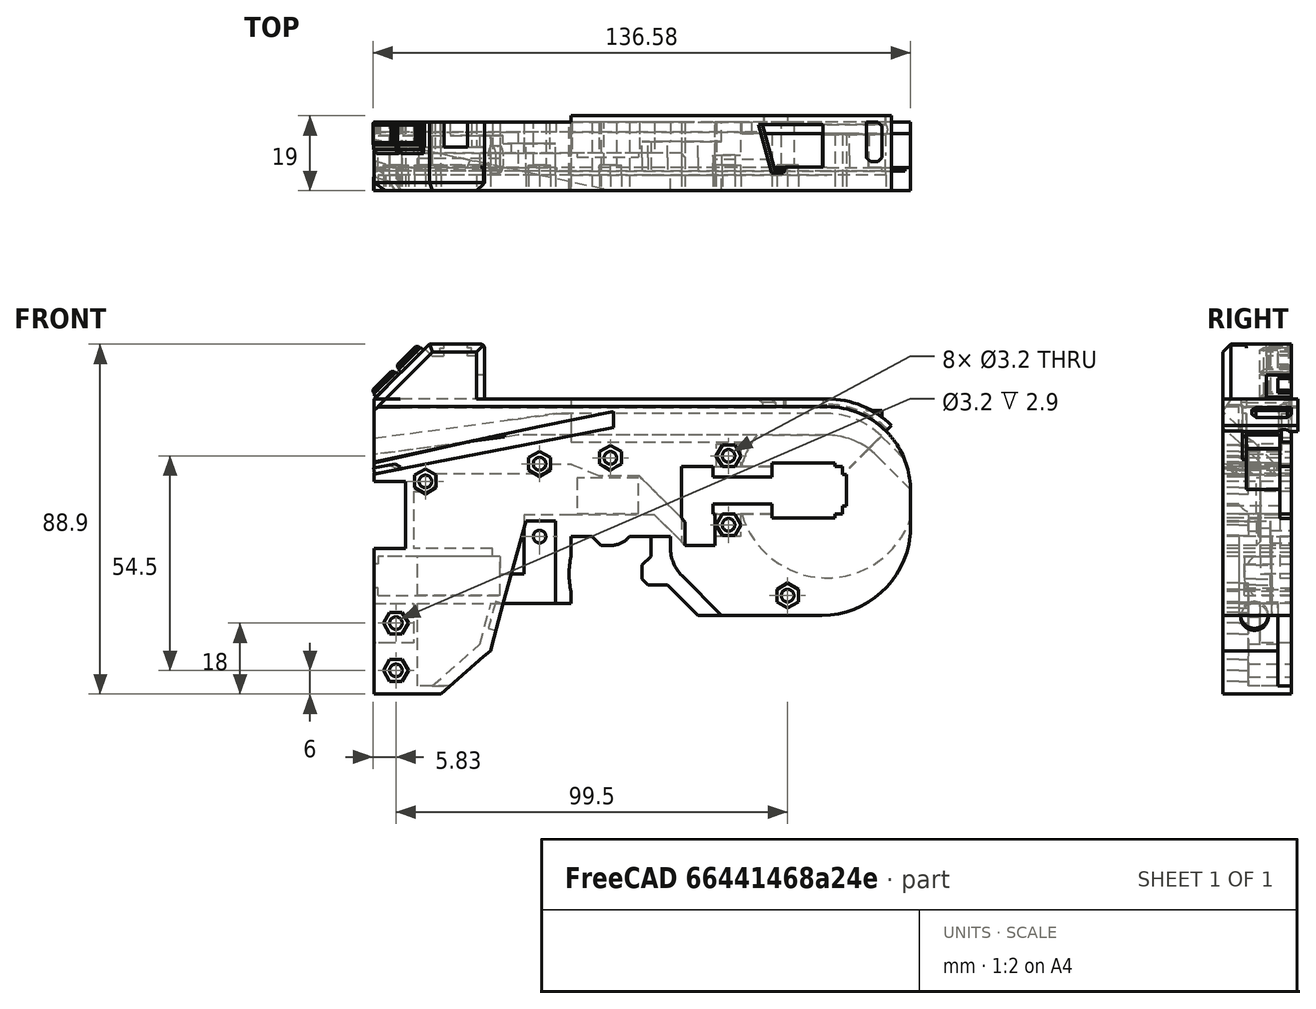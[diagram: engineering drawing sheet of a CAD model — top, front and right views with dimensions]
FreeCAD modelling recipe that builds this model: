
FCSTD DOCUMENT  (FreeCAD 0.20R29603 (Git))
Label: frame
License: All rights reserved
LicenseURL: http://en.wikipedia.org/wiki/All_rights_reserved
objects: Sketcher::SketchObject×74, PartDesign::Pocket×73, PartDesign::Pad×30, PartDesign::Plane×10, PartDesign::Chamfer×10, PartDesign::Groove×4, PartDesign::Fillet×3, PartDesign::Body×1
note: 325 computed .brp shape members not serialized (recipe doc carries the construction recipe); baked Part::Feature solids carry a one-line shape summary decoded from their .brp

FEATURE [Sketcher::SketchObject] Sketch
  FullyConstrained = true
  MapMode = 5
  Placement = pos=(0,0,0) rot=(1,0,0;1.5708rad)
  Support = -> [XZ_Plane]
  sketch-geometry (25):
    g0: LineSegment StartX=32.25 StartY=-20 StartZ=0 EndX=86.25 EndY=-20 EndZ=0
    g1: LineSegment StartX=65 StartY=33 StartZ=0 EndX=-50 EndY=33 EndZ=0
    g2: LineSegment StartX=-50 StartY=33 StartZ=0 EndX=-50 EndY=-40 EndZ=0
    g3: ArcOfCircle CenterX=65 CenterY=11.75 CenterZ=0 NormalX=0 NormalY=0 NormalZ=1 AngleXU=0 Radius=21.25 StartAngle=6.28319 EndAngle=7.85398
    g4: LineSegment StartX=86.25 StartY=11.75 StartZ=0 EndX=86.25 EndY=-20 EndZ=0
    g5: LineSegment StartX=1.8e-15 StartY=0 StartZ=0 EndX=5.375 EndY=0 EndZ=0
    g6: LineSegment StartX=5.375 StartY=0 StartZ=0 EndX=7.625 EndY=-2.25 EndZ=0
    g7: LineSegment StartX=7.625 StartY=-2.25 StartZ=0 EndX=12.625 EndY=-2.25 EndZ=0
    g8: LineSegment StartX=12.625 StartY=-2.25 StartZ=0 EndX=14.875 EndY=0 EndZ=0
    g9: LineSegment StartX=14.875 StartY=0 StartZ=0 EndX=20.25 EndY=0 EndZ=0
    g10: LineSegment StartX=20.25 StartY=0 StartZ=0 EndX=20.25 EndY=-5 EndZ=0
    g11: LineSegment StartX=20.25 StartY=-5 StartZ=0 EndX=18 EndY=-7.25 EndZ=0
    g12: LineSegment StartX=18 StartY=-7.25 StartZ=0 EndX=18 EndY=-10.75 EndZ=0
    g13: LineSegment StartX=18 StartY=-10.75 StartZ=0 EndX=19.5 EndY=-12.25 EndZ=0
    g14: LineSegment StartX=19.5 StartY=-12.25 StartZ=0 EndX=24.5 EndY=-12.25 EndZ=0
    g15: LineSegment StartX=24.5 StartY=-12.25 StartZ=0 EndX=32.25 EndY=-20 EndZ=0
    g16: LineSegment StartX=1.8e-15 StartY=0 StartZ=0 EndX=1.8e-15 EndY=-4 EndZ=0
    g17: ArcOfCircle CenterX=-10 CenterY=-4.5 CenterZ=0 NormalX=0 NormalY=0 NormalZ=1 AngleXU=0 Radius=10.0125 StartAngle=6.23323 EndAngle=6.33314
    g18: ArcOfCircle CenterX=20 CenterY=-9.5 CenterZ=0 NormalX=0 NormalY=0 NormalZ=1 AngleXU=0 Radius=20.5 StartAngle=2.92028 EndAngle=3.36291
    g19: LineSegment StartX=-50 StartY=-40 StartZ=0 EndX=0 EndY=-40 EndZ=0
    g20: LineSegment StartX=0 StartY=-14 StartZ=0 EndX=0 EndY=-40 EndZ=0
    g21: Circle CenterX=-44.5 CenterY=-34 CenterZ=0 NormalX=0 NormalY=0 NormalZ=1 AngleXU=0 Radius=1.6
    g22: Circle CenterX=-8 CenterY=1.1e-15 CenterZ=0 NormalX=0 NormalY=0 NormalZ=1 AngleXU=0 Radius=1.6
    g23: Circle CenterX=-37 CenterY=14 CenterZ=0 NormalX=0 NormalY=0 NormalZ=1 AngleXU=0 Radius=1.6
    g24: Circle CenterX=-8 CenterY=18.5 CenterZ=0 NormalX=0 NormalY=0 NormalZ=1 AngleXU=0 Radius=1.6
  constraints (78):
    c: PointOnObject(g9,g-1)
    c: Horizontal(g0)
    c: Horizontal(g1)
    c: Coincident(g1,g2)
    c: Vertical(g2)
    c: DistanceX(g-1,g9) = 20.25
    c: DistanceY(g0,g9) = 20
    c: DistanceY(g-1,g1) = 33
    c: Coincident(g4,g3)
    c: Coincident(g4,g0)
    c: Vertical(g4)
    c: Coincident(g1,g3)
    c: Tangent(g1,g3)
    c: DistanceX(g-1,g3) = 65
    c: Tangent(g3,g4)
    c: DistanceY(g-1,g3) = 11.75
    c: PointOnObject(g5,g-1)
    c: Horizontal(g5)
    c: Coincident(g5,g6)
    c: Coincident(g6,g7)
    c: Horizontal(g7)
    c: Coincident(g7,g8)
    c: PointOnObject(g8,g-1)
    c: Coincident(g8,g9)
    c: DistanceX(g5,g8) = 9.5
    c: DistanceX(g5,g5) = 5.375
    c: DistanceY(g6,g5) = 2.25
    c: Angle(g5,g6) = 2.35619
    c: Angle(g8,g9) = 2.35619
    c: Coincident(g9,g10)
    c: Vertical(g10)
    c: Coincident(g10,g11)
    c: Coincident(g11,g12)
    c: Vertical(g12)
    c: Coincident(g12,g13)
    c: Coincident(g13,g14)
    c: Horizontal(g14)
    c: Coincident(g14,g15)
    c: Coincident(g15,g0)
    c: Angle(g0,g15) = 2.35619
    c: DistanceY(g10,g10) = 5
    c: DistanceY(g12,g12) = 3.5
    c: Angle(g10,g11) = 2.35619
    c: DistanceX(g11,g10) = 2.25
    c: DistanceX(g12,g13) = 1.5
    c: Angle(g13,g12) = 2.35619
    c: DistanceX(g14,g14) = 5
    c: Coincident(g5,g16)
    c: PointOnObject(g16,g-2)
    c: Vertical(g16)
    c: DistanceY(g16,g16) = 4
    c: Coincident(g17,g16)
    c: PointOnObject(g17,g-2)
    c: Coincident(g18,g17)
    c: DistanceY(g17,g16) = 1
    c: DistanceX(g17,g16) = 10
    c: PointOnObject(g18,g-2)
    c: DistanceY(g18,g17) = 9
    c: DistanceX(g18,g18) = 20
    c: Coincident(g19,g2)
    c: Horizontal(g19)
    c: DistanceX(g2,g5) = 50
    c: PointOnObject(g19,g-2)
    c: Coincident(g20,g18)
    c: Coincident(g20,g19)
    c: DistanceY(g19,g5) = 40
    c: Diameter(g24) = 3.2
    c: Diameter(g23) = 3.2
    c: Diameter(g21) = 3.2
    c: Diameter(g22) = 3.2
    c: DistanceX(g21,g19) = 44.5
    c: DistanceY(g19,g21) = 6
    c: DistanceX(g22,g19) = 8
    c: DistanceY(g19,g22) = 40
    c: DistanceX(g23,g19) = 37
    c: DistanceY(g19,g23) = 54
    c: DistanceY(g19,g24) = 58.5
    c: DistanceX(g24,g19) = 8
FEATURE [PartDesign::Pad] Pad
  Direction = (1,1,1)
  Length = 15
  Length2 = 100
  Placement = pos=(0,0,0) rot=(1,0,0;1.5708rad)
  Profile = -> Sketch
  Type = 0
FEATURE [Sketcher::SketchObject] Sketch001
  FullyConstrained = false
  MapMode = 5
  Placement = pos=(0,0,0) rot=(1,0,0;1.5708rad)
  Support = -> [XZ_Plane]
  sketch-geometry (4):
    g0: LineSegment StartX=117.233 StartY=-40 StartZ=0 EndX=-50 EndY=-40 EndZ=0
    g1: LineSegment StartX=-50 StartY=-40 StartZ=0 EndX=-50 EndY=33 EndZ=0
    g2: LineSegment StartX=-50 StartY=33 StartZ=0 EndX=117.233 EndY=33 EndZ=0
    g3: LineSegment StartX=117.233 StartY=33 StartZ=0 EndX=117.233 EndY=-40 EndZ=0
  constraints (11):
    c: Coincident(g0,g1)
    c: Coincident(g1,g2)
    c: Coincident(g2,g3)
    c: Coincident(g3,g0)
    c: Horizontal(g0)
    c: Horizontal(g2)
    c: Vertical(g1)
    c: Vertical(g3)
    c: DistanceY(g-1,g2) = 33
    c: DistanceY(g0,g-1) = 40
    c: DistanceX(g1,g-1) = 50
FEATURE [PartDesign::Pocket] Pocket
  BaseFeature = -> Pad
  Direction = (1,1,1)
  Length = 1.6
  Length2 = 100
  Placement = pos=(0,0,0) rot=(1,0,0;1.5708rad)
  Profile = -> Sketch001
  Reversed = true
  Type = 0
FEATURE [Sketcher::SketchObject] Sketch003
  FullyConstrained = true
  MapMode = 5
  Placement = pos=(0,0,0) rot=(1,0,0;1.5708rad)
  Support = -> [XZ_Plane]
  sketch-geometry (1):
    g0: Circle CenterX=65 CenterY=12 CenterZ=0 NormalX=0 NormalY=0 NormalZ=1 AngleXU=0 Radius=22.5
  constraints (3):
    c: Diameter(g0) = 45
    c: DistanceX(g-1,g0) = 65
    c: DistanceY(g-1,g0) = 12
FEATURE [Sketcher::SketchObject] Sketch004
  FullyConstrained = true
  MapMode = 5
  Placement = pos=(0,0,0) rot=(1,0,0;1.5708rad)
  Support = -> [XZ_Plane]
  sketch-geometry (16):
    g0: LineSegment StartX=29 StartY=17.75 StartZ=0 EndX=51 EndY=17.75 EndZ=0
    g1: LineSegment StartX=51 StartY=17.75 StartZ=0 EndX=51 EndY=18.75 EndZ=0
    g2: LineSegment StartX=51 StartY=18.75 StartZ=0 EndX=67 EndY=18.75 EndZ=0
    g3: LineSegment StartX=67 StartY=18.75 StartZ=0 EndX=67 EndY=17.75 EndZ=0
    g4: LineSegment StartX=67 StartY=17.75 StartZ=0 EndX=69 EndY=17.75 EndZ=0
    g5: LineSegment StartX=69 StartY=17.75 StartZ=0 EndX=69 EndY=15.75 EndZ=0
    g6: LineSegment StartX=69 StartY=15.75 StartZ=0 EndX=70 EndY=15.75 EndZ=0
    g7: LineSegment StartX=70 StartY=15.75 StartZ=0 EndX=70 EndY=7.75 EndZ=0
    g8: LineSegment StartX=70 StartY=7.75 StartZ=0 EndX=69 EndY=7.75 EndZ=0
    g9: LineSegment StartX=69 StartY=7.75 StartZ=0 EndX=69 EndY=5.75 EndZ=0
    g10: LineSegment StartX=69 StartY=5.75 StartZ=0 EndX=67 EndY=5.75 EndZ=0
    g11: LineSegment StartX=67 StartY=5.75 StartZ=0 EndX=67 EndY=4.75 EndZ=0
    g12: LineSegment StartX=67 StartY=4.75 StartZ=0 EndX=51 EndY=4.75 EndZ=0
    g13: LineSegment StartX=51 StartY=4.75 StartZ=0 EndX=51 EndY=5.75 EndZ=0
    g14: LineSegment StartX=51 StartY=5.75 StartZ=0 EndX=29 EndY=5.75 EndZ=0
    g15: LineSegment StartX=29 StartY=17.75 StartZ=0 EndX=29 EndY=5.75 EndZ=0
  constraints (48):
    c: Horizontal(g0)
    c: Coincident(g0,g1)
    c: Vertical(g1)
    c: Coincident(g1,g2)
    c: Horizontal(g2)
    c: Coincident(g2,g3)
    c: Vertical(g3)
    c: Coincident(g3,g4)
    c: Horizontal(g4)
    c: Coincident(g4,g5)
    c: Vertical(g5)
    c: Coincident(g5,g6)
    c: Horizontal(g6)
    c: Coincident(g6,g7)
    c: Vertical(g7)
    c: Coincident(g7,g8)
    c: Horizontal(g8)
    c: Coincident(g8,g9)
    c: Vertical(g9)
    c: Coincident(g9,g10)
    c: Horizontal(g10)
    c: Coincident(g10,g11)
    c: Vertical(g11)
    c: Coincident(g11,g12)
    c: Horizontal(g12)
    c: Coincident(g12,g13)
    c: Vertical(g13)
    c: Coincident(g13,g14)
    c: Horizontal(g14)
    c: DistanceY(g14,g0) = 12
    c: DistanceX(g1,g4) = 18
    c: DistanceX(g4,g4) = 2
    c: DistanceY(g5,g5) = 2
    c: PointOnObject(g0,g4)
    c: DistanceY(g1,g1) = 1
    c: DistanceX(g6,g6) = 1
    c: DistanceX(g10,g10) = 2
    c: DistanceX(g12,g9) = 18
    c: PointOnObject(g13,g1)
    c: DistanceY(g13,g13) = 1
    c: DistanceY(g9,g9) = 2
    c: PointOnObject(g10,g14)
    c: DistanceX(g0,g0) = 22
    c: Coincident(g0,g15)
    c: Vertical(g15)
    c: DistanceX(g-1,g13) = 51
    c: DistanceY(g-1,g13) = 5.75
    c: Coincident(g15,g14)
FEATURE [Sketcher::SketchObject] Sketch005
  FullyConstrained = false
  MapMode = 5
  Placement = pos=(0,0,0) rot=(0.57735,0.57735,0.57735;2.0944rad)
  Support = -> [YZ_Plane]
  sketch-geometry (5):
    g0: Circle CenterX=-10 CenterY=11.7 CenterZ=0 NormalX=0 NormalY=0 NormalZ=1 AngleXU=0 Radius=6.05
    g1: ArcOfCircle CenterX=-10 CenterY=11.7 CenterZ=0 NormalX=0 NormalY=0 NormalZ=1 AngleXU=0 Radius=6.05 StartAngle=1.5708 EndAngle=4.71239
    g2: LineSegment StartX=-10 StartY=17.75 StartZ=0 EndX=-16.4104 EndY=17.75 EndZ=0
    g3: LineSegment StartX=-16.4104 StartY=17.75 StartZ=0 EndX=-16.4104 EndY=5.65 EndZ=0
    g4: LineSegment StartX=-16.4104 StartY=5.65 StartZ=0 EndX=-10 EndY=5.65 EndZ=0
  constraints (14):
    c: DistanceX(g0,g-1) = 10
    c: Diameter(g0) = 12.1
    c: DistanceY(g-1,g0) = 11.7
    c: Coincident(g1,g0)
    c: PointOnObject(g1,g0)
    c: Coincident(g1,g2)
    c: Coincident(g2,g3)
    c: Vertical(g3)
    c: Coincident(g3,g4)
    c: Coincident(g4,g1)
    c: Tangent(g4,g0)
    c: Horizontal(g4)
    c: Horizontal(g2)
    c: Tangent(g2,g0)
FEATURE [Sketcher::SketchObject] Sketch006
  FullyConstrained = false
  MapMode = 5
  Placement = pos=(0,0,0) rot=(0.57735,0.57735,0.57735;2.0944rad)
  Support = -> [YZ_Plane]
  sketch-geometry (4):
    g0: LineSegment StartX=-25.4908 StartY=23.3679 StartZ=0 EndX=-15 EndY=23.3679 EndZ=0
    g1: LineSegment StartX=-15 StartY=23.3679 StartZ=0 EndX=-15 EndY=0.094988 EndZ=0
    g2: LineSegment StartX=-15 StartY=0.094988 StartZ=0 EndX=-25.4908 EndY=0.094988 EndZ=0
    g3: LineSegment StartX=-25.4908 StartY=0.094988 StartZ=0 EndX=-25.4908 EndY=23.3679 EndZ=0
  constraints (9):
    c: Coincident(g0,g1)
    c: Coincident(g1,g2)
    c: Coincident(g2,g3)
    c: Coincident(g3,g0)
    c: Horizontal(g0)
    c: Horizontal(g2)
    c: Vertical(g1)
    c: Vertical(g3)
    c: DistanceX(g1,g-1) = 15
FEATURE [Sketcher::SketchObject] Sketch007
  FullyConstrained = true
  MapMode = 5
  Placement = pos=(0,0,0) rot=(1,0,0;1.5708rad)
  Support = -> [XZ_Plane]
  sketch-geometry (6):
    g0: LineSegment StartX=-12 StartY=-5 StartZ=0 EndX=-50 EndY=-5 EndZ=0
    g1: LineSegment StartX=-50 StartY=-5 StartZ=0 EndX=-50 EndY=-15 EndZ=0
    g2: LineSegment StartX=-50 StartY=-15 StartZ=0 EndX=-18 EndY=-15 EndZ=0
    g3: LineSegment StartX=-18 StartY=-15 StartZ=0 EndX=-18 EndY=-9.5 EndZ=0
    g4: LineSegment StartX=-18 StartY=-9.5 StartZ=0 EndX=-12 EndY=-9.5 EndZ=0
    g5: LineSegment StartX=-12 StartY=-9.5 StartZ=0 EndX=-12 EndY=-5 EndZ=0
  constraints (18):
    c: Coincident(g0,g1)
    c: Coincident(g1,g2)
    c: Horizontal(g0)
    c: Horizontal(g2)
    c: Vertical(g1)
    c: DistanceY(g2,g0) = 10
    c: DistanceY(g0,g-1) = 5
    c: DistanceX(g0,g-1) = 50
    c: Coincident(g2,g3)
    c: Vertical(g3)
    c: Coincident(g3,g4)
    c: Horizontal(g4)
    c: Coincident(g4,g5)
    c: Vertical(g5)
    c: DistanceX(g2,g2) = 32
    c: DistanceX(g5,g-1) = 12
    c: Coincident(g0,g5)
    c: DistanceY(g5,g5) = 4.5
FEATURE [Sketcher::SketchObject] Sketch008
  FullyConstrained = true
  MapMode = 5
  Placement = pos=(0,0,0) rot=(1,0,0;1.5708rad)
  Support = -> [XZ_Plane]
  sketch-geometry (4):
    g0: LineSegment StartX=-50 StartY=-3 StartZ=0 EndX=-42 EndY=-3 EndZ=0
    g1: LineSegment StartX=-42 StartY=-3 StartZ=0 EndX=-42 EndY=14 EndZ=0
    g2: LineSegment StartX=-42 StartY=14 StartZ=0 EndX=-50 EndY=14 EndZ=0
    g3: LineSegment StartX=-50 StartY=14 StartZ=0 EndX=-50 EndY=-3 EndZ=0
  constraints (12):
    c: Coincident(g0,g1)
    c: Coincident(g1,g2)
    c: Coincident(g2,g3)
    c: Coincident(g3,g0)
    c: Horizontal(g0)
    c: Horizontal(g2)
    c: Vertical(g1)
    c: Vertical(g3)
    c: DistanceX(g0,g0) = 8
    c: DistanceY(g1,g1) = 17
    c: DistanceY(g0,g-1) = 3
    c: DistanceX(g0,g-1) = 50
FEATURE [Sketcher::SketchObject] Sketch009
  FullyConstrained = true
  MapMode = 5
  Placement = pos=(0,0,0) rot=(1,0,0;1.5708rad)
  Support = -> [XZ_Plane]
  sketch-geometry (4):
    g0: LineSegment StartX=-50 StartY=-17 StartZ=0 EndX=-40 EndY=-17 EndZ=0
    g1: LineSegment StartX=-40 StartY=-27 StartZ=0 EndX=-50 EndY=-27 EndZ=0
    g2: LineSegment StartX=-50 StartY=-27 StartZ=0 EndX=-50 EndY=-17 EndZ=0
    g3: LineSegment StartX=-40 StartY=-17 StartZ=0 EndX=-40 EndY=-27 EndZ=0
  constraints (12):
    c: Horizontal(g0)
    c: Horizontal(g1)
    c: Coincident(g1,g2)
    c: Coincident(g2,g0)
    c: Vertical(g2)
    c: Vertical(g3)
    c: DistanceY(g2,g2) = 10
    c: DistanceX(g0,g3) = 10
    c: DistanceX(g1,g-1) = 50
    c: DistanceY(g0,g-1) = 17
    c: Coincident(g0,g3)
    c: Coincident(g1,g3)
FEATURE [Sketcher::SketchObject] Sketch010
  FullyConstrained = true
  MapMode = 5
  Placement = pos=(0,0,0) rot=(1,0,0;1.5708rad)
  Support = -> [XZ_Plane]
  sketch-geometry (4):
    g0: LineSegment StartX=-40 StartY=-17 StartZ=0 EndX=-45 EndY=-17 EndZ=0
    g1: LineSegment StartX=-45 StartY=-17 StartZ=0 EndX=-45 EndY=-27 EndZ=0
    g2: LineSegment StartX=-45 StartY=-27 StartZ=0 EndX=-40 EndY=-27 EndZ=0
    g3: LineSegment StartX=-40 StartY=-27 StartZ=0 EndX=-40 EndY=-17 EndZ=0
  constraints (12):
    c: Coincident(g0,g1)
    c: Coincident(g1,g2)
    c: Coincident(g2,g3)
    c: Coincident(g3,g0)
    c: Horizontal(g0)
    c: Horizontal(g2)
    c: Vertical(g1)
    c: Vertical(g3)
    c: DistanceY(g1,g1) = 10
    c: DistanceX(g0,g0) = 5
    c: DistanceY(g0,g-1) = 17
    c: DistanceX(g0,g-1) = 40
FEATURE [PartDesign::Plane] DatumPlane002
  AttachmentOffset = pos=(0,0,-115) rot=(0,0,1;0rad)
  Length = 102.234
  MapMode = 5
  Placement = pos=(65,0,2.55e-14) rot=(0.707107,0,-0.707107;3.14159rad)
  ResizeMode = 0
  Support = -> [Pocket]
  Width = 63.3342
FEATURE [Sketcher::SketchObject] Sketch002
  FullyConstrained = true
  MapMode = 5
  Placement = pos=(65,0,2.55e-14) rot=(0.707107,0,-0.707107;3.14159rad)
  Support = -> [DatumPlane002]
  sketch-geometry (8):
    g0: LineSegment StartX=-33 StartY=10.1 StartZ=0 EndX=-31.75 EndY=10.1 EndZ=0
    g1: LineSegment StartX=-31.75 StartY=1.6 StartZ=0 EndX=-33 EndY=1.6 EndZ=0
    g2: LineSegment StartX=-31.75 StartY=1.6 StartZ=0 EndX=-31.75 EndY=4.1 EndZ=0
    g3: LineSegment StartX=-31.75 StartY=4.1 StartZ=0 EndX=-29.75 EndY=4.1 EndZ=0
    g4: LineSegment StartX=-29.75 StartY=4.1 StartZ=0 EndX=-29.75 EndY=9.1 EndZ=0
    g5: LineSegment StartX=-29.75 StartY=9.1 StartZ=0 EndX=-31.75 EndY=9.1 EndZ=0
    g6: LineSegment StartX=-31.75 StartY=9.1 StartZ=0 EndX=-31.75 EndY=10.1 EndZ=0
    g7: LineSegment StartX=-33 StartY=1.6 StartZ=0 EndX=-33 EndY=10.1 EndZ=0
  constraints (24):
    c: Horizontal(g0)
    c: Horizontal(g1)
    c: Coincident(g1,g2)
    c: Vertical(g2)
    c: Coincident(g2,g3)
    c: Horizontal(g3)
    c: Coincident(g3,g4)
    c: Vertical(g4)
    c: Coincident(g4,g5)
    c: Horizontal(g5)
    c: Coincident(g5,g6)
    c: Coincident(g6,g0)
    c: Vertical(g6)
    c: DistanceX(g1,g1) = 1.25
    c: DistanceY(g2,g2) = 2.5
    c: DistanceY(g4,g4) = 5
    c: DistanceY(g1,g0) = 8.5
    c: DistanceX(g3,g3) = 2
    c: PointOnObject(g5,g2)
    c: DistanceY(g-1,g1) = 1.6
    c: DistanceX(g1,g-1) = 33
    c: Coincident(g7,g1)
    c: Coincident(g7,g0)
    c: Vertical(g7)
FEATURE [PartDesign::Pocket] Pocket001
  BaseFeature = -> Pocket
  Direction = (1,1,1)
  Length = 115
  Length2 = 100
  Placement = pos=(0,0,0) rot=(1,0,0;1.5708rad)
  Profile = -> Sketch002
  Reversed = true
  Type = 0
FEATURE [Sketcher::SketchObject] Sketch014
  FullyConstrained = true
  MapMode = 5
  Placement = pos=(65,0,2.55e-14) rot=(0.707107,0,-0.707107;3.14159rad)
  Support = -> [DatumPlane002]
  expr: Constraints[100] = Sketch002.Constraints[21]
  expr: Constraints[101] = Sketch002.Constraints[21]
  expr: Constraints[102] = Sketch002.Constraints[21]
  expr: Constraints[121] = Sketch002.Constraints[13]
  expr: Constraints[122] = Sketch002.Constraints[14]
  expr: Constraints[123] = Sketch002.Constraints[15]
  expr: Constraints[124] = Sketch002.Constraints[16]
  expr: Constraints[125] = Sketch002.Constraints[17]
  expr: Constraints[127] = Sketch002.Constraints[19]
  expr: Constraints[128] = Sketch002.Constraints[20]
  expr: Constraints[136] = Sketch002.Constraints[21]
  expr: Constraints[137] = Sketch002.Constraints[21]
  expr: Constraints[138] = Sketch002.Constraints[21]
  expr: Constraints[13] = Sketch002.Constraints[13]
  expr: Constraints[14] = Sketch002.Constraints[14]
  expr: Constraints[157] = Sketch002.Constraints[13]
  expr: Constraints[158] = Sketch002.Constraints[14]
  expr: Constraints[159] = Sketch002.Constraints[15]
  expr: Constraints[15] = Sketch002.Constraints[15]
  expr: Constraints[160] = Sketch002.Constraints[16]
  expr: Constraints[161] = Sketch002.Constraints[17]
  expr: Constraints[163] = Sketch002.Constraints[19]
  expr: Constraints[164] = Sketch002.Constraints[20]
  expr: Constraints[16] = Sketch002.Constraints[16]
  expr: Constraints[172] = Sketch002.Constraints[21]
  expr: Constraints[173] = Sketch002.Constraints[21]
  expr: Constraints[174] = Sketch002.Constraints[21]
  expr: Constraints[17] = Sketch002.Constraints[17]
  expr: Constraints[193] = Sketch002.Constraints[13]
  expr: Constraints[194] = Sketch002.Constraints[14]
  expr: Constraints[195] = Sketch002.Constraints[15]
  expr: Constraints[196] = Sketch002.Constraints[16]
  expr: Constraints[197] = Sketch002.Constraints[17]
  expr: Constraints[199] = Sketch002.Constraints[19]
  expr: Constraints[19] = Sketch002.Constraints[19]
  expr: Constraints[200] = Sketch002.Constraints[20]
  expr: Constraints[208] = Sketch002.Constraints[21]
  expr: Constraints[209] = Sketch002.Constraints[21]
  expr: Constraints[20] = Sketch002.Constraints[20]
  expr: Constraints[210] = Sketch002.Constraints[21]
  expr: Constraints[229] = Sketch002.Constraints[13]
  expr: Constraints[230] = Sketch002.Constraints[14]
  expr: Constraints[231] = Sketch002.Constraints[15]
  expr: Constraints[232] = Sketch002.Constraints[16]
  expr: Constraints[233] = Sketch002.Constraints[17]
  expr: Constraints[235] = Sketch002.Constraints[19]
  expr: Constraints[236] = Sketch002.Constraints[20]
  expr: Constraints[244] = Sketch002.Constraints[21]
  expr: Constraints[245] = Sketch002.Constraints[21]
  expr: Constraints[246] = Sketch002.Constraints[21]
  expr: Constraints[28] = Sketch002.Constraints[21]
  expr: Constraints[29] = Sketch002.Constraints[21]
  expr: Constraints[30] = Sketch002.Constraints[21]
  expr: Constraints[49] = Sketch002.Constraints[13]
  expr: Constraints[50] = Sketch002.Constraints[14]
  expr: Constraints[51] = Sketch002.Constraints[15]
  expr: Constraints[52] = Sketch002.Constraints[16]
  expr: Constraints[53] = Sketch002.Constraints[17]
  expr: Constraints[55] = Sketch002.Constraints[19]
  expr: Constraints[56] = Sketch002.Constraints[20]
  expr: Constraints[64] = Sketch002.Constraints[21]
  expr: Constraints[65] = Sketch002.Constraints[21]
  expr: Constraints[66] = Sketch002.Constraints[21]
  expr: Constraints[85] = Sketch002.Constraints[13]
  expr: Constraints[86] = Sketch002.Constraints[14]
  expr: Constraints[87] = Sketch002.Constraints[15]
  expr: Constraints[88] = Sketch002.Constraints[16]
  expr: Constraints[89] = Sketch002.Constraints[17]
  expr: Constraints[91] = Sketch002.Constraints[19]
  expr: Constraints[92] = Sketch002.Constraints[20]
  sketch-geometry (84):
    g0: LineSegment StartX=-33 StartY=10.1 StartZ=0 EndX=-31.75 EndY=10.1 EndZ=0
    g1: LineSegment StartX=-31.75 StartY=1.6 StartZ=0 EndX=-33 EndY=1.6 EndZ=0
    g2: LineSegment StartX=-31.75 StartY=1.6 StartZ=0 EndX=-31.75 EndY=4.1 EndZ=0
    g3: LineSegment StartX=-31.75 StartY=4.1 StartZ=0 EndX=-29.75 EndY=4.1 EndZ=0
    g4: LineSegment StartX=-29.75 StartY=4.1 StartZ=0 EndX=-29.75 EndY=9.1 EndZ=0
    g5: LineSegment StartX=-29.75 StartY=9.1 StartZ=0 EndX=-31.75 EndY=9.1 EndZ=0
    g6: LineSegment StartX=-31.75 StartY=9.1 StartZ=0 EndX=-31.75 EndY=10.1 EndZ=0
    g7: LineSegment StartX=-33 StartY=10.1 StartZ=0 EndX=-33 EndY=1.6 EndZ=0
    g8: LineSegment StartX=-33 StartY=1.6 StartZ=0 EndX=-33 EndY=1.6 EndZ=0
    g9: LineSegment StartX=-33 StartY=1.6 StartZ=0 EndX=-33 EndY=1.6 EndZ=0
    g10: LineSegment StartX=-33 StartY=1.6 StartZ=0 EndX=-33 EndY=1.6 EndZ=0
    g11: LineSegment StartX=-33 StartY=1.6 StartZ=0 EndX=-33 EndY=1.6 EndZ=0
    g12: LineSegment StartX=-33 StartY=10.1 StartZ=0 EndX=-31.75 EndY=10.1 EndZ=0
    g13: LineSegment StartX=-31.75 StartY=1.6 StartZ=0 EndX=-33 EndY=1.6 EndZ=0
    g14: LineSegment StartX=-31.75 StartY=1.6 StartZ=0 EndX=-31.75 EndY=4.1 EndZ=0
    g15: LineSegment StartX=-31.75 StartY=4.1 StartZ=0 EndX=-29.75 EndY=4.1 EndZ=0
    g16: LineSegment StartX=-29.75 StartY=4.1 StartZ=0 EndX=-29.75 EndY=9.1 EndZ=0
    g17: LineSegment StartX=-29.75 StartY=9.1 StartZ=0 EndX=-31.75 EndY=9.1 EndZ=0
    g18: LineSegment StartX=-31.75 StartY=9.1 StartZ=0 EndX=-31.75 EndY=10.1 EndZ=0
    g19: LineSegment StartX=-33 StartY=10.1 StartZ=0 EndX=-33 EndY=1.6 EndZ=0
    g20: LineSegment StartX=-33 StartY=1.6 StartZ=0 EndX=-33 EndY=1.6 EndZ=0
    g21: LineSegment StartX=-33 StartY=1.6 StartZ=0 EndX=-33 EndY=1.6 EndZ=0
    g22: LineSegment StartX=-33 StartY=1.6 StartZ=0 EndX=-33 EndY=1.6 EndZ=0
    g23: LineSegment StartX=-33 StartY=1.6 StartZ=0 EndX=-33 EndY=1.6 EndZ=0
    g24: LineSegment StartX=-33 StartY=10.1 StartZ=0 EndX=-31.75 EndY=10.1 EndZ=0
    g25: LineSegment StartX=-31.75 StartY=1.6 StartZ=0 EndX=-33 EndY=1.6 EndZ=0
    g26: LineSegment StartX=-31.75 StartY=1.6 StartZ=0 EndX=-31.75 EndY=4.1 EndZ=0
    g27: LineSegment StartX=-31.75 StartY=4.1 StartZ=0 EndX=-29.75 EndY=4.1 EndZ=0
    g28: LineSegment StartX=-29.75 StartY=4.1 StartZ=0 EndX=-29.75 EndY=9.1 EndZ=0
    g29: LineSegment StartX=-29.75 StartY=9.1 StartZ=0 EndX=-31.75 EndY=9.1 EndZ=0
    g30: LineSegment StartX=-31.75 StartY=9.1 StartZ=0 EndX=-31.75 EndY=10.1 EndZ=0
    g31: LineSegment StartX=-33 StartY=10.1 StartZ=0 EndX=-33 EndY=1.6 EndZ=0
    g32: LineSegment StartX=-33 StartY=1.6 StartZ=0 EndX=-33 EndY=1.6 EndZ=0
    g33: LineSegment StartX=-33 StartY=1.6 StartZ=0 EndX=-33 EndY=1.6 EndZ=0
    g34: LineSegment StartX=-33 StartY=1.6 StartZ=0 EndX=-33 EndY=1.6 EndZ=0
    g35: LineSegment StartX=-33 StartY=1.6 StartZ=0 EndX=-33 EndY=1.6 EndZ=0
    g36: LineSegment StartX=-33 StartY=10.1 StartZ=0 EndX=-31.75 EndY=10.1 EndZ=0
    g37: LineSegment StartX=-31.75 StartY=1.6 StartZ=0 EndX=-33 EndY=1.6 EndZ=0
    g38: LineSegment StartX=-31.75 StartY=1.6 StartZ=0 EndX=-31.75 EndY=4.1 EndZ=0
    g39: LineSegment StartX=-31.75 StartY=4.1 StartZ=0 EndX=-29.75 EndY=4.1 EndZ=0
    g40: LineSegment StartX=-29.75 StartY=4.1 StartZ=0 EndX=-29.75 EndY=9.1 EndZ=0
    g41: LineSegment StartX=-29.75 StartY=9.1 StartZ=0 EndX=-31.75 EndY=9.1 EndZ=0
    g42: LineSegment StartX=-31.75 StartY=9.1 StartZ=0 EndX=-31.75 EndY=10.1 EndZ=0
    g43: LineSegment StartX=-33 StartY=10.1 StartZ=0 EndX=-33 EndY=1.6 EndZ=0
    g44: LineSegment StartX=-33 StartY=1.6 StartZ=0 EndX=-33 EndY=1.6 EndZ=0
    g45: LineSegment StartX=-33 StartY=1.6 StartZ=0 EndX=-33 EndY=1.6 EndZ=0
    g46: LineSegment StartX=-33 StartY=1.6 StartZ=0 EndX=-33 EndY=1.6 EndZ=0
    g47: LineSegment StartX=-33 StartY=1.6 StartZ=0 EndX=-33 EndY=1.6 EndZ=0
    g48: LineSegment StartX=-33 StartY=10.1 StartZ=0 EndX=-31.75 EndY=10.1 EndZ=0
    g49: LineSegment StartX=-31.75 StartY=1.6 StartZ=0 EndX=-33 EndY=1.6 EndZ=0
    g50: LineSegment StartX=-31.75 StartY=1.6 StartZ=0 EndX=-31.75 EndY=4.1 EndZ=0
    g51: LineSegment StartX=-31.75 StartY=4.1 StartZ=0 EndX=-29.75 EndY=4.1 EndZ=0
    g52: LineSegment StartX=-29.75 StartY=4.1 StartZ=0 EndX=-29.75 EndY=9.1 EndZ=0
    g53: LineSegment StartX=-29.75 StartY=9.1 StartZ=0 EndX=-31.75 EndY=9.1 EndZ=0
    g54: LineSegment StartX=-31.75 StartY=9.1 StartZ=0 EndX=-31.75 EndY=10.1 EndZ=0
    g55: LineSegment StartX=-33 StartY=10.1 StartZ=0 EndX=-33 EndY=1.6 EndZ=0
    g56: LineSegment StartX=-33 StartY=1.6 StartZ=0 EndX=-33 EndY=1.6 EndZ=0
    g57: LineSegment StartX=-33 StartY=1.6 StartZ=0 EndX=-33 EndY=1.6 EndZ=0
    g58: LineSegment StartX=-33 StartY=1.6 StartZ=0 EndX=-33 EndY=1.6 EndZ=0
    g59: LineSegment StartX=-33 StartY=1.6 StartZ=0 EndX=-33 EndY=1.6 EndZ=0
    g60: LineSegment StartX=-33 StartY=10.1 StartZ=0 EndX=-31.75 EndY=10.1 EndZ=0
    g61: LineSegment StartX=-31.75 StartY=1.6 StartZ=0 EndX=-33 EndY=1.6 EndZ=0
    g62: LineSegment StartX=-31.75 StartY=1.6 StartZ=0 EndX=-31.75 EndY=4.1 EndZ=0
    g63: LineSegment StartX=-31.75 StartY=4.1 StartZ=0 EndX=-29.75 EndY=4.1 EndZ=0
    g64: LineSegment StartX=-29.75 StartY=4.1 StartZ=0 EndX=-29.75 EndY=9.1 EndZ=0
    g65: LineSegment StartX=-29.75 StartY=9.1 StartZ=0 EndX=-31.75 EndY=9.1 EndZ=0
    g66: LineSegment StartX=-31.75 StartY=9.1 StartZ=0 EndX=-31.75 EndY=10.1 EndZ=0
    g67: LineSegment StartX=-33 StartY=10.1 StartZ=0 EndX=-33 EndY=1.6 EndZ=0
    g68: LineSegment StartX=-33 StartY=1.6 StartZ=0 EndX=-33 EndY=1.6 EndZ=0
    g69: LineSegment StartX=-33 StartY=1.6 StartZ=0 EndX=-33 EndY=1.6 EndZ=0
    g70: LineSegment StartX=-33 StartY=1.6 StartZ=0 EndX=-33 EndY=1.6 EndZ=0
    g71: LineSegment StartX=-33 StartY=1.6 StartZ=0 EndX=-33 EndY=1.6 EndZ=0
    g72: LineSegment StartX=-33 StartY=10.1 StartZ=0 EndX=-31.75 EndY=10.1 EndZ=0
    g73: LineSegment StartX=-31.75 StartY=1.6 StartZ=0 EndX=-33 EndY=1.6 EndZ=0
    g74: LineSegment StartX=-31.75 StartY=1.6 StartZ=0 EndX=-31.75 EndY=4.1 EndZ=0
    g75: LineSegment StartX=-31.75 StartY=4.1 StartZ=0 EndX=-29.75 EndY=4.1 EndZ=0
    g76: LineSegment StartX=-29.75 StartY=4.1 StartZ=0 EndX=-29.75 EndY=9.1 EndZ=0
    g77: LineSegment StartX=-29.75 StartY=9.1 StartZ=0 EndX=-31.75 EndY=9.1 EndZ=0
    g78: LineSegment StartX=-31.75 StartY=9.1 StartZ=0 EndX=-31.75 EndY=10.1 EndZ=0
    g79: LineSegment StartX=-33 StartY=10.1 StartZ=0 EndX=-33 EndY=1.6 EndZ=0
    g80: LineSegment StartX=-33 StartY=1.6 StartZ=0 EndX=-33 EndY=1.6 EndZ=0
    g81: LineSegment StartX=-33 StartY=1.6 StartZ=0 EndX=-33 EndY=1.6 EndZ=0
    g82: LineSegment StartX=-33 StartY=1.6 StartZ=0 EndX=-33 EndY=1.6 EndZ=0
    g83: LineSegment StartX=-33 StartY=1.6 StartZ=0 EndX=-33 EndY=1.6 EndZ=0
  constraints (252):
    c: Horizontal(g0)
    c: Horizontal(g1)
    c: Coincident(g1,g2)
    c: Vertical(g2)
    c: Coincident(g2,g3)
    c: Horizontal(g3)
    c: Coincident(g3,g4)
    c: Vertical(g4)
    c: Coincident(g4,g5)
    c: Horizontal(g5)
    c: Coincident(g5,g6)
    c: Coincident(g6,g0)
    c: Vertical(g6)
    c: DistanceX(g1,g1) = 1.25
    c: DistanceY(g2,g2) = 2.5
    c: DistanceY(g4,g4) = 5
    c: DistanceY(g1,g0) = 8.5
    c: DistanceX(g3,g3) = 2
    c: PointOnObject(g5,g2)
    c: DistanceY(g-1,g1) = 1.6
    c: DistanceX(g1,g-1) = 33
    c: Coincident(g0,g7)
    c: Vertical(g7)
    c: Coincident(g7,g8)
    c: Horizontal(g8)
    c: Coincident(g8,g9)
    c: Vertical(g9)
    c: PointOnObject(g1,g7)
    c: DistanceY(g9,g9) = 0
    c: DistanceX(g9,g1) = 0
    c: DistanceY(g9,g1) = 0
    c: Coincident(g9,g10)
    c: Horizontal(g10)
    c: Coincident(g10,g11)
    c: Coincident(g11,g1)
    c: Vertical(g11)
    c: Horizontal(g12)
    c: Horizontal(g13)
    c: Coincident(g13,g14)
    c: Vertical(g14)
    c: Coincident(g14,g15)
    c: Horizontal(g15)
    c: Coincident(g15,g16)
    c: Vertical(g16)
    c: Coincident(g16,g17)
    c: Horizontal(g17)
    c: Coincident(g17,g18)
    c: Coincident(g18,g12)
    c: Vertical(g18)
    c: DistanceX(g13,g13) = 1.25
    c: DistanceY(g14,g14) = 2.5
    c: DistanceY(g16,g16) = 5
    c: DistanceY(g13,g12) = 8.5
    c: DistanceX(g15,g15) = 2
    c: PointOnObject(g17,g14)
    c: DistanceY(g-1,g13) = 1.6
    c: DistanceX(g13,g-1) = 33
    c: Coincident(g12,g19)
    c: Vertical(g19)
    c: Coincident(g19,g20)
    c: Horizontal(g20)
    c: Coincident(g20,g21)
    c: Vertical(g21)
    c: PointOnObject(g13,g19)
    c: DistanceY(g21,g21) = 0
    c: DistanceX(g21,g13) = 0
    c: DistanceY(g21,g13) = 0
    c: Coincident(g21,g22)
    c: Horizontal(g22)
    c: Coincident(g22,g23)
    c: Coincident(g23,g13)
    c: Vertical(g23)
    c: Horizontal(g24)
    c: Horizontal(g25)
    c: Coincident(g25,g26)
    c: Vertical(g26)
    c: Coincident(g26,g27)
    c: Horizontal(g27)
    c: Coincident(g27,g28)
    c: Vertical(g28)
    c: Coincident(g28,g29)
    c: Horizontal(g29)
    c: Coincident(g29,g30)
    c: Coincident(g30,g24)
    c: Vertical(g30)
    c: DistanceX(g25,g25) = 1.25
    c: DistanceY(g26,g26) = 2.5
    c: DistanceY(g28,g28) = 5
    c: DistanceY(g25,g24) = 8.5
    c: DistanceX(g27,g27) = 2
    c: PointOnObject(g29,g26)
    c: DistanceY(g-1,g25) = 1.6
    c: DistanceX(g25,g-1) = 33
    c: Coincident(g24,g31)
    c: Vertical(g31)
    c: Coincident(g31,g32)
    c: Horizontal(g32)
    c: Coincident(g32,g33)
    c: Vertical(g33)
    c: PointOnObject(g25,g31)
    c: DistanceY(g33,g33) = 0
    c: DistanceX(g33,g25) = 0
    c: DistanceY(g33,g25) = 0
    c: Coincident(g33,g34)
    c: Horizontal(g34)
    c: Coincident(g34,g35)
    c: Coincident(g35,g25)
    c: Vertical(g35)
    c: Horizontal(g36)
    c: Horizontal(g37)
    c: Coincident(g37,g38)
    c: Vertical(g38)
    c: Coincident(g38,g39)
    c: Horizontal(g39)
    c: Coincident(g39,g40)
    c: Vertical(g40)
    c: Coincident(g40,g41)
    c: Horizontal(g41)
    c: Coincident(g41,g42)
    c: Coincident(g42,g36)
    c: Vertical(g42)
    c: DistanceX(g37,g37) = 1.25
    c: DistanceY(g38,g38) = 2.5
    c: DistanceY(g40,g40) = 5
    c: DistanceY(g37,g36) = 8.5
    c: DistanceX(g39,g39) = 2
    c: PointOnObject(g41,g38)
    c: DistanceY(g-1,g37) = 1.6
    c: DistanceX(g37,g-1) = 33
    c: Coincident(g36,g43)
    c: Vertical(g43)
    c: Coincident(g43,g44)
    c: Horizontal(g44)
    c: Coincident(g44,g45)
    c: Vertical(g45)
    c: PointOnObject(g37,g43)
    c: DistanceY(g45,g45) = 0
    c: DistanceX(g45,g37) = 0
    c: DistanceY(g45,g37) = 0
    c: Coincident(g45,g46)
    c: Horizontal(g46)
    c: Coincident(g46,g47)
    c: Coincident(g47,g37)
    c: Vertical(g47)
    c: Horizontal(g48)
    c: Horizontal(g49)
    c: Coincident(g49,g50)
    c: Vertical(g50)
    c: Coincident(g50,g51)
    c: Horizontal(g51)
    c: Coincident(g51,g52)
    c: Vertical(g52)
    c: Coincident(g52,g53)
    c: Horizontal(g53)
    c: Coincident(g53,g54)
    c: Coincident(g54,g48)
    c: Vertical(g54)
    c: DistanceX(g49,g49) = 1.25
    c: DistanceY(g50,g50) = 2.5
    c: DistanceY(g52,g52) = 5
    c: DistanceY(g49,g48) = 8.5
    c: DistanceX(g51,g51) = 2
    c: PointOnObject(g53,g50)
    c: DistanceY(g-1,g49) = 1.6
    c: DistanceX(g49,g-1) = 33
    c: Coincident(g48,g55)
    c: Vertical(g55)
    c: Coincident(g55,g56)
    c: Horizontal(g56)
    c: Coincident(g56,g57)
    c: Vertical(g57)
    c: PointOnObject(g49,g55)
    c: DistanceY(g57,g57) = 0
    c: DistanceX(g57,g49) = 0
    c: DistanceY(g57,g49) = 0
    c: Coincident(g57,g58)
    c: Horizontal(g58)
    c: Coincident(g58,g59)
    c: Coincident(g59,g49)
    c: Vertical(g59)
    c: Horizontal(g60)
    c: Horizontal(g61)
    c: Coincident(g61,g62)
    c: Vertical(g62)
    c: Coincident(g62,g63)
    c: Horizontal(g63)
    c: Coincident(g63,g64)
    c: Vertical(g64)
    c: Coincident(g64,g65)
    c: Horizontal(g65)
    c: Coincident(g65,g66)
    c: Coincident(g66,g60)
    c: Vertical(g66)
    c: DistanceX(g61,g61) = 1.25
    c: DistanceY(g62,g62) = 2.5
    c: DistanceY(g64,g64) = 5
    c: DistanceY(g61,g60) = 8.5
    c: DistanceX(g63,g63) = 2
    c: PointOnObject(g65,g62)
    c: DistanceY(g-1,g61) = 1.6
    c: DistanceX(g61,g-1) = 33
    c: Coincident(g60,g67)
    c: Vertical(g67)
    c: Coincident(g67,g68)
    c: Horizontal(g68)
    c: Coincident(g68,g69)
    c: Vertical(g69)
    c: PointOnObject(g61,g67)
    c: DistanceY(g69,g69) = 0
    c: DistanceX(g69,g61) = 0
    c: DistanceY(g69,g61) = 0
    c: Coincident(g69,g70)
    c: Horizontal(g70)
    c: Coincident(g70,g71)
    c: Coincident(g71,g61)
    c: Vertical(g71)
    c: Horizontal(g72)
    c: Horizontal(g73)
    c: Coincident(g73,g74)
    c: Vertical(g74)
    c: Coincident(g74,g75)
    c: Horizontal(g75)
    c: Coincident(g75,g76)
    c: Vertical(g76)
    c: Coincident(g76,g77)
    c: Horizontal(g77)
    c: Coincident(g77,g78)
    c: Coincident(g78,g72)
    c: Vertical(g78)
    c: DistanceX(g73,g73) = 1.25
    c: DistanceY(g74,g74) = 2.5
    c: DistanceY(g76,g76) = 5
    c: DistanceY(g73,g72) = 8.5
    c: DistanceX(g75,g75) = 2
    c: PointOnObject(g77,g74)
    c: DistanceY(g-1,g73) = 1.6
    c: DistanceX(g73,g-1) = 33
    c: Coincident(g72,g79)
    c: Vertical(g79)
    c: Coincident(g79,g80)
    c: Horizontal(g80)
    c: Coincident(g80,g81)
    c: Vertical(g81)
    c: PointOnObject(g73,g79)
    c: DistanceY(g81,g81) = 0
    c: DistanceX(g81,g73) = 0
    c: DistanceY(g81,g73) = 0
    c: Coincident(g81,g82)
    c: Horizontal(g82)
    c: Coincident(g82,g83)
    c: Coincident(g83,g73)
    c: Vertical(g83)
FEATURE [Sketcher::SketchObject] Sketch015
  FullyConstrained = false
  MapMode = 5
  Placement = pos=(65,0,2.55e-14) rot=(0.707107,0,-0.707107;3.14159rad)
  Support = -> [DatumPlane002]
  sketch-geometry (1):
    g0: LineSegment StartX=-11.75 StartY=-5 StartZ=0 EndX=-11.75 EndY=20.7526 EndZ=0
  constraints (3):
    c: Vertical(g0)
    c: DistanceY(g0,g-1) = 5
    c: DistanceX(g0,g-1) = 11.75
FEATURE [PartDesign::Groove] Groove
  Angle = 45
  Axis = (0,-1,-2e-16)
  Base = (65,5,11.75)
  BaseFeature = -> Pocket001
  Placement = pos=(0,0,0) rot=(1,0,0;1.5708rad)
  Profile = -> Sketch014
  ReferenceAxis = -> Sketch015 [Edge1]
  Reversed = true
FEATURE [Sketcher::SketchObject] Sketch017
  FullyConstrained = false
  MapMode = 5
  Placement = pos=(0,0,0) rot=(1,0,0;1.5708rad)
  Support = -> [XZ_Plane]
  sketch-geometry (5):
    g0: LineSegment StartX=-50 StartY=25 StartZ=0 EndX=0 EndY=31.75 EndZ=0
    g1: LineSegment StartX=0 StartY=31.75 StartZ=0 EndX=0 EndY=35.9961 EndZ=0
    g2: LineSegment StartX=0 StartY=35.9961 StartZ=0 EndX=-55.6372 EndY=35.9961 EndZ=0
    g3: LineSegment StartX=-55.6372 StartY=35.9961 StartZ=0 EndX=-55.6372 EndY=25 EndZ=0
    g4: LineSegment StartX=-55.6372 StartY=25 StartZ=0 EndX=-50 EndY=25 EndZ=0
  constraints (13):
    c: PointOnObject(g0,g-2)
    c: Coincident(g0,g1)
    c: PointOnObject(g1,g-2)
    c: Coincident(g1,g2)
    c: Horizontal(g2)
    c: Coincident(g2,g3)
    c: Vertical(g3)
    c: Coincident(g3,g4)
    c: Coincident(g4,g0)
    c: Horizontal(g4)
    c: DistanceY(g-1,g0) = 25
    c: DistanceX(g0,g-1) = 50
    c: DistanceY(g-1,g0) = 31.75
FEATURE [PartDesign::Plane] DatumPlane003  label="right-wall"
  Length = 158.62
  MapMode = 5
  Placement = pos=(0,-15,-2e-15) rot=(1,0,0;1.5708rad)
  ResizeMode = 0
  Width = 110.938
FEATURE [Sketcher::SketchObject] Sketch018
  FullyConstrained = true
  MapMode = 5
  Placement = pos=(0,-15,-2e-15) rot=(1,0,0;1.5708rad)
  Support = -> [DatumPlane003]
  sketch-geometry (4):
    g0: LineSegment StartX=-52 StartY=15.5 StartZ=0 EndX=-8 EndY=24 EndZ=0
    g1: LineSegment StartX=-8 StartY=24 StartZ=0 EndX=-8 EndY=28 EndZ=0
    g2: LineSegment StartX=-8 StartY=28 StartZ=0 EndX=-52 EndY=18.5 EndZ=0
    g3: LineSegment StartX=-52 StartY=18.5 StartZ=0 EndX=-52 EndY=15.5 EndZ=0
  constraints (12):
    c: Coincident(g0,g1)
    c: Coincident(g1,g2)
    c: Coincident(g2,g3)
    c: Coincident(g3,g0)
    c: Vertical(g3)
    c: Vertical(g1)
    c: DistanceX(g0,g-1) = 52
    c: DistanceY(g3,g3) = 3
    c: DistanceY(g-1,g0) = 15.5
    c: DistanceY(g1,g1) = 4
    c: DistanceY(g-1,g0) = 24
    c: DistanceX(g0,g-1) = 8
FEATURE [Sketcher::SketchObject] Sketch019
  FullyConstrained = true
  MapMode = 5
  Placement = pos=(0,0,0) rot=(1,0,0;1.5708rad)
  Support = -> [XZ_Plane]
  sketch-geometry (4):
    g0: LineSegment StartX=37 StartY=23.5 StartZ=0 EndX=43 EndY=23.5 EndZ=0
    g1: LineSegment StartX=43 StartY=23.5 StartZ=0 EndX=43 EndY=0 EndZ=0
    g2: LineSegment StartX=43 StartY=0 StartZ=0 EndX=37 EndY=0 EndZ=0
    g3: LineSegment StartX=37 StartY=0 StartZ=0 EndX=37 EndY=23.5 EndZ=0
  constraints (12):
    c: Coincident(g0,g1)
    c: Coincident(g1,g2)
    c: Coincident(g2,g3)
    c: Coincident(g3,g0)
    c: Horizontal(g0)
    c: Horizontal(g2)
    c: Vertical(g1)
    c: Vertical(g3)
    c: DistanceY(g3,g3) = 23.5
    c: DistanceX(g0,g0) = 6
    c: DistanceX(g-1,g2) = 37
    c: PointOnObject(g2,g-1)
FEATURE [Sketcher::SketchObject] Sketch020
  FullyConstrained = true
  MapMode = 5
  Placement = pos=(0,0,0) rot=(1,0,0;1.5708rad)
  Support = -> [XZ_Plane]
  sketch-geometry (3):
    g0: Circle CenterX=40 CenterY=20.5 CenterZ=0 NormalX=0 NormalY=0 NormalZ=1 AngleXU=0 Radius=1.6
    g1: Circle CenterX=40 CenterY=3 CenterZ=0 NormalX=0 NormalY=0 NormalZ=1 AngleXU=0 Radius=1.6
    g2: LineSegment StartX=40 StartY=20.5 StartZ=0 EndX=40 EndY=3 EndZ=0
  constraints (8):
    c: Diameter(g0) = 3.2
    c: Diameter(g1) = 3.2
    c: Coincident(g2,g0)
    c: Coincident(g2,g1)
    c: Vertical(g2)
    c: DistanceX(g-1,g1) = 40
    c: DistanceY(g2,g2) = 17.5
    c: DistanceY(g-1,g1) = 3
FEATURE [Sketcher::SketchObject] Sketch021
  FullyConstrained = true
  MapMode = 5
  Placement = pos=(0,-15,-2e-15) rot=(1,0,0;1.5708rad)
  Support = -> [DatumPlane003]
  sketch-geometry (15):
    g0: LineSegment StartX=41.5877 StartY=17.75 StartZ=0 EndX=43.1754 EndY=20.5 EndZ=0
    g1: LineSegment StartX=43.1754 StartY=20.5 StartZ=0 EndX=41.5877 EndY=23.25 EndZ=0
    g2: LineSegment StartX=41.5877 StartY=23.25 StartZ=0 EndX=38.4123 EndY=23.25 EndZ=0
    g3: LineSegment StartX=38.4123 StartY=23.25 StartZ=0 EndX=36.8246 EndY=20.5 EndZ=0
    g4: LineSegment StartX=36.8246 StartY=20.5 StartZ=0 EndX=38.4123 EndY=17.75 EndZ=0
    g5: LineSegment StartX=38.4123 StartY=17.75 StartZ=0 EndX=41.5877 EndY=17.75 EndZ=0
    g6: Circle CenterX=40 CenterY=20.5 CenterZ=0 NormalX=0 NormalY=0 NormalZ=1 AngleXU=0 Radius=3.17543
    g7: LineSegment StartX=41.5877 StartY=0.25 StartZ=0 EndX=43.1754 EndY=3 EndZ=0
    g8: LineSegment StartX=43.1754 StartY=3 StartZ=0 EndX=41.5877 EndY=5.75 EndZ=0
    g9: LineSegment StartX=41.5877 StartY=5.75 StartZ=0 EndX=38.4123 EndY=5.75 EndZ=0
    g10: LineSegment StartX=38.4123 StartY=5.75 StartZ=0 EndX=36.8246 EndY=3 EndZ=0
    g11: LineSegment StartX=36.8246 StartY=3 StartZ=0 EndX=38.4123 EndY=0.25 EndZ=0
    g12: LineSegment StartX=38.4123 StartY=0.25 StartZ=0 EndX=41.5877 EndY=0.25 EndZ=0
    g13: Circle CenterX=40 CenterY=3 CenterZ=0 NormalX=0 NormalY=0 NormalZ=1 AngleXU=0 Radius=3.17543
    g14: LineSegment StartX=40 StartY=20.5 StartZ=0 EndX=40 EndY=3 EndZ=0
  constraints (36):
    c: Coincident(g0,g1)
    c: Coincident(g1,g2)
    c: Coincident(g2,g3)
    c: Coincident(g3,g4)
    c: Coincident(g4,g5)
    c: Coincident(g5,g0)
    c: Equal(g0, g1-g5) x5
    c: PointOnObject(g0,g6)
    c: PointOnObject(g1,g6)
    c: PointOnObject(g2,g6)
    c: PointOnObject(g3,g6)
    c: PointOnObject(g4,g6)
    c: PointOnObject(g5,g6)
    c: Coincident(g7,g8)
    c: Coincident(g8,g9)
    c: Coincident(g9,g10)
    c: Coincident(g10,g11)
    c: Coincident(g11,g12)
    c: Coincident(g12,g7)
    c: Equal(g7, g8-g12) x5
    c: PointOnObject(g7,g13)
    c: PointOnObject(g8,g13)
    c: PointOnObject(g9,g13)
    c: PointOnObject(g10,g13)
    c: PointOnObject(g11,g13)
    c: PointOnObject(g12,g13)
    c: Horizontal(g2)
    c: DistanceY(g4,g2) = 5.5
    c: DistanceY(g11,g9) = 5.5
    c: Coincident(g14,g6)
    c: Coincident(g14,g13)
    c: Vertical(g14)
    c: DistanceY(g14,g14) = 17.5
    c: DistanceX(g-1,g13) = 40
    c: DistanceY(g-1,g13) = 3
    c: Horizontal(g9)
FEATURE [Sketcher::SketchObject] Sketch022
  FullyConstrained = true
  MapMode = 5
  Placement = pos=(0,0,0) rot=(1,0,0;1.5708rad)
  Support = -> [XZ_Plane]
FEATURE [PartDesign::Plane] DatumPlane004
  Length = 177.297
  MapMode = 5
  Placement = pos=(26.625,-3.4e-15,-26.625) rot=(-0.382683,0,0.92388;3.14159rad)
  ResizeMode = 0
  Support = -> [Groove]
  Width = 67.8572
FEATURE [Sketcher::SketchObject] Sketch016
  FullyConstrained = true
  MapMode = 5
  Placement = pos=(26.625,-3.4e-15,-26.625) rot=(-0.382683,0,0.92388;3.14159rad)
  Support = -> [DatumPlane004]
  expr: Constraints[13] = Sketch002.Constraints[13]
  expr: Constraints[14] = Sketch002.Constraints[14]
  expr: Constraints[15] = Sketch002.Constraints[15]
  expr: Constraints[16] = Sketch002.Constraints[16]
  expr: Constraints[17] = Sketch002.Constraints[17]
  expr: Constraints[19] = Sketch002.Constraints[19]
  sketch-geometry (8):
    g0: LineSegment StartX=-75.525 StartY=10.1 StartZ=0 EndX=-74.275 EndY=10.1 EndZ=0
    g1: LineSegment StartX=-74.275 StartY=1.6 StartZ=0 EndX=-75.525 EndY=1.6 EndZ=0
    g2: LineSegment StartX=-74.275 StartY=1.6 StartZ=0 EndX=-74.275 EndY=4.1 EndZ=0
    g3: LineSegment StartX=-74.275 StartY=4.1 StartZ=0 EndX=-72.275 EndY=4.1 EndZ=0
    g4: LineSegment StartX=-72.275 StartY=4.1 StartZ=0 EndX=-72.275 EndY=9.1 EndZ=0
    g5: LineSegment StartX=-72.275 StartY=9.1 StartZ=0 EndX=-74.275 EndY=9.1 EndZ=0
    g6: LineSegment StartX=-74.275 StartY=9.1 StartZ=0 EndX=-74.275 EndY=10.1 EndZ=0
    g7: LineSegment StartX=-75.525 StartY=1.6 StartZ=0 EndX=-75.525 EndY=10.1 EndZ=0
  constraints (24):
    c: Horizontal(g0)
    c: Horizontal(g1)
    c: Coincident(g1,g2)
    c: Vertical(g2)
    c: Coincident(g2,g3)
    c: Horizontal(g3)
    c: Coincident(g3,g4)
    c: Vertical(g4)
    c: Coincident(g4,g5)
    c: Horizontal(g5)
    c: Coincident(g5,g6)
    c: Coincident(g6,g0)
    c: Vertical(g6)
    c: DistanceX(g1,g1) = 1.25
    c: DistanceY(g2,g2) = 2.5
    c: DistanceY(g4,g4) = 5
    c: DistanceY(g1,g0) = 8.5
    c: DistanceX(g3,g3) = 2
    c: PointOnObject(g5,g2)
    c: DistanceY(g-1,g1) = 1.6
    c: Coincident(g7,g1)
    c: Coincident(g7,g0)
    c: Vertical(g7)
    c: DistanceX(g1,g-1) = 75.525
FEATURE [PartDesign::Pocket] Pocket009
  BaseFeature = -> Groove
  Direction = (1,1,1)
  Length = 15
  Length2 = 100
  Placement = pos=(0,0,0) rot=(1,0,0;1.5708rad)
  Profile = -> Sketch016
  Type = 0
FEATURE [PartDesign::Pocket] Pocket002
  BaseFeature = -> Pocket009
  Direction = (1,1,1)
  Length = 4.5
  Length2 = 100
  Placement = pos=(0,0,0) rot=(1,0,0;1.5708rad)
  Profile = -> Sketch003
  Reversed = true
  Type = 0
FEATURE [PartDesign::Pocket] Pocket003
  BaseFeature = -> Pocket002
  Direction = (1,1,1)
  Length = 15
  Length2 = 100
  Placement = pos=(0,0,0) rot=(1,0,0;1.5708rad)
  Profile = -> Sketch004
  Reversed = true
  Type = 0
FEATURE [PartDesign::Pad] Pad001
  BaseFeature = -> Pocket003
  Direction = (1,1,1)
  Length = 51
  Length2 = 100
  Placement = pos=(0,0,0) rot=(1,0,0;1.5708rad)
  Profile = -> Sketch005
  Type = 0
FEATURE [PartDesign::Pocket] Pocket004
  BaseFeature = -> Pad001
  Direction = (1,1,1)
  Length = 8
  Length2 = 100
  Placement = pos=(0,0,0) rot=(1,0,0;1.5708rad)
  Profile = -> Sketch006
  Reversed = true
  Type = 1
FEATURE [PartDesign::Pocket] Pocket005
  BaseFeature = -> Pocket004
  Direction = (1,1,1)
  Length = 13.6
  Length2 = 100
  Placement = pos=(0,0,0) rot=(1,0,0;1.5708rad)
  Profile = -> Sketch007
  Reversed = true
  Type = 0
FEATURE [PartDesign::Pocket] Pocket006
  BaseFeature = -> Pocket005
  Direction = (1,1,1)
  Length = 15
  Length2 = 100
  Placement = pos=(0,0,0) rot=(1,0,0;1.5708rad)
  Profile = -> Sketch008
  Reversed = true
  Type = 0
FEATURE [PartDesign::Pocket] Pocket007
  BaseFeature = -> Pocket006
  Direction = (1,1,1)
  Length = 9.6
  Length2 = 100
  Placement = pos=(0,0,0) rot=(1,0,0;1.5708rad)
  Profile = -> Sketch009
  Reversed = true
  Type = 0
FEATURE [PartDesign::Pocket] Pocket008
  BaseFeature = -> Pocket007
  Direction = (1,1,1)
  Length = 11.6
  Length2 = 100
  Placement = pos=(0,0,0) rot=(1,0,0;1.5708rad)
  Profile = -> Sketch010
  Reversed = true
  Type = 0
FEATURE [PartDesign::Plane] DatumPlane  label="film-motor-base-plane"
  Length = 102.234
  MapMode = 5
  Placement = pos=(-18,0,0) rot=(0.707107,0,-0.707107;3.14159rad)
  ResizeMode = 0
  Support = -> [Pocket008]
  Width = 63.3342
FEATURE [Sketcher::SketchObject] Sketch011
  FullyConstrained = true
  MapMode = 5
  Placement = pos=(-18,0,0) rot=(0.707107,0,-0.707107;3.14159rad)
  Support = -> [DatumPlane]
  sketch-geometry (4):
    g0: ArcOfCircle CenterX=10 CenterY=7.6 CenterZ=0 NormalX=0 NormalY=0 NormalZ=1 AngleXU=0 Radius=6 StartAngle=0.585686 EndAngle=2.55591
    g1: LineSegment StartX=5 StartY=15 StartZ=0 EndX=5 EndY=10.9166 EndZ=0
    g2: LineSegment StartX=15 StartY=15 StartZ=0 EndX=15 EndY=10.9166 EndZ=0
    g3: LineSegment StartX=15 StartY=15 StartZ=0 EndX=5 EndY=15 EndZ=0
  constraints (13):
    c: DistanceX(g-1,g2) = 15
    c: DistanceY(g-1,g2) = 15
    c: DistanceX(g1,g2) = 10
    c: DistanceX(g0,g2) = 5
    c: DistanceY(g0,g2) = 7.4
    c: Vertical(g1)
    c: Coincident(g0,g1)
    c: Vertical(g2)
    c: Coincident(g3,g2)
    c: Coincident(g3,g1)
    c: Horizontal(g3)
    c: Coincident(g2,g0)
    c: Diameter(g0) = 12
FEATURE [PartDesign::Pad] Pad002
  BaseFeature = -> Pocket008
  Direction = (1,1,1)
  Length = 21
  Length2 = 100
  Placement = pos=(0,0,0) rot=(1,0,0;1.5708rad)
  Profile = -> Sketch011
  Type = 0
FEATURE [PartDesign::Pocket] Pocket010
  BaseFeature = -> Pad002
  Direction = (1,1,1)
  Length = 0
  Length2 = 100
  Placement = pos=(0,0,0) rot=(1,0,0;1.5708rad)
  Profile = -> Sketch017
  Reversed = true
  Type = 3
  UpToFace = -> Pad002 [Face60]
FEATURE [PartDesign::Fillet] Fillet
  Base = -> Pocket010 [Edge129,Edge131,Edge127]
  BaseFeature = -> Pocket010
  Placement = pos=(0,0,0) rot=(1,0,0;1.5708rad)
  Radius = 20
  SupportTransform = false
  UseAllEdges = false
FEATURE [PartDesign::Chamfer] Chamfer
  Angle = 45
  Base = -> Fillet [Edge69]
  BaseFeature = -> Fillet
  ChamferType = 0
  FlipDirection = false
  Placement = pos=(0,0,0) rot=(1,0,0;1.5708rad)
  Size = 1
  Size2 = 20
  SupportTransform = false
  UseAllEdges = false
FEATURE [PartDesign::Groove] Groove001
  Angle = 12
  Axis = (0,-2e-16,1)
  Base = (-8,-15,24)
  BaseFeature = -> Chamfer
  Placement = pos=(0,0,0) rot=(1,0,0;1.5708rad)
  Profile = -> Sketch018
  ReferenceAxis = -> Sketch018 [Edge2]
  Reversed = true
FEATURE [PartDesign::Pocket] Pocket011
  BaseFeature = -> Groove001
  Direction = (1,1,1)
  Length = 10
  Length2 = 100
  Placement = pos=(0,0,0) rot=(1,0,0;1.5708rad)
  Profile = -> Sketch019
  Reversed = true
  Type = 0
FEATURE [PartDesign::Pocket] Pocket012
  BaseFeature = -> Pocket011
  Direction = (1,1,1)
  Length = 15
  Length2 = 100
  Placement = pos=(0,0,0) rot=(1,0,0;1.5708rad)
  Profile = -> Sketch020
  Reversed = true
  Type = 0
FEATURE [PartDesign::Pocket] Pocket013
  BaseFeature = -> Pocket012
  Direction = (1,1,1)
  Length = 2.5
  Length2 = 100
  Placement = pos=(0,0,0) rot=(1,0,0;1.5708rad)
  Profile = -> Sketch021
  Type = 0
FEATURE [Sketcher::SketchObject] Sketch024
  FullyConstrained = false
  MapMode = 5
  Placement = pos=(0,0,0) rot=(1,0,0;1.5708rad)
  Support = -> [XZ_Plane]
  sketch-geometry (6):
    g0: LineSegment StartX=36 StartY=5.75 StartZ=0 EndX=36 EndY=17.75 EndZ=0
    g1: LineSegment StartX=36 StartY=17.75 StartZ=0 EndX=29 EndY=17.75 EndZ=0
    g2: LineSegment StartX=29 StartY=17.75 StartZ=0 EndX=29 EndY=-2.25 EndZ=0
    g3: LineSegment StartX=36 StartY=5.75 StartZ=0 EndX=36 EndY=5.75 EndZ=0
    g4: LineSegment StartX=36 StartY=5.75 StartZ=0 EndX=36 EndY=-2.25 EndZ=0
    g5: LineSegment StartX=36 StartY=-2.25 StartZ=0 EndX=29 EndY=-2.25 EndZ=0
  constraints (17):
    c: Coincident(g0,g1)
    c: Coincident(g1,g2)
    c: Horizontal(g1)
    c: Vertical(g0)
    c: Vertical(g2)
    c: DistanceX(g2,g0) = 7
    c: Coincident(g0,g3)
    c: Horizontal(g3)
    c: Coincident(g3,g4)
    c: Vertical(g4)
    c: Coincident(g4,g5)
    c: Coincident(g5,g2)
    c: Horizontal(g5)
    c: DistanceY(g4,g4) = 8
    c: DistanceY(g-1,g1) = 17.75
    c: DistanceY(g0,g0) = 12
    c: DistanceX(g5,g5) = 7
FEATURE [PartDesign::Pocket] Pocket015
  BaseFeature = -> Pocket013
  Direction = (1,1,1)
  Length = 15
  Length2 = 100
  Placement = pos=(0,0,0) rot=(1,0,0;1.5708rad)
  Profile = -> Sketch024
  Reversed = true
  Type = 0
FEATURE [Sketcher::SketchObject] Sketch025
  FullyConstrained = true
  MapMode = 5
  Placement = pos=(0,-15,-2e-15) rot=(1,0,0;1.5708rad)
  Support = -> [DatumPlane003]
  sketch-geometry (10):
    g0: LineSegment StartX=0 StartY=34.99 StartZ=0 EndX=65 EndY=34.99 EndZ=0
    g1: ArcOfCircle CenterX=65 CenterY=11.75 CenterZ=0 NormalX=0 NormalY=0 NormalZ=1 AngleXU=0 Radius=23.24 StartAngle=0.785398 EndAngle=1.5708
    g2: ArcOfCircle CenterX=65 CenterY=11.75 CenterZ=0 NormalX=0 NormalY=0 NormalZ=1 AngleXU=0 Radius=21.24 StartAngle=0.785398 EndAngle=1.5708
    g3: LineSegment StartX=0 StartY=32.99 StartZ=0 EndX=65 EndY=32.99 EndZ=0
    g4: LineSegment StartX=65 StartY=11.75 StartZ=0 EndX=81.4332 EndY=28.1832 EndZ=0
    g5: LineSegment StartX=65 StartY=32.99 StartZ=0 EndX=65 EndY=11.75 EndZ=0
    g6: LineSegment StartX=80.0189 StartY=26.7689 StartZ=0 EndX=81.4332 EndY=28.1832 EndZ=0
    g7: LineSegment StartX=0 StartY=32.99 StartZ=0 EndX=-49 EndY=32.99 EndZ=0
    g8: LineSegment StartX=-49 StartY=32.99 StartZ=0 EndX=-47 EndY=34.99 EndZ=0
    g9: LineSegment StartX=-47 StartY=34.99 StartZ=0 EndX=0 EndY=34.99 EndZ=0
  constraints (29):
    c: Horizontal(g0)
    c: Coincident(g1,g0)
    c: Coincident(g3,g2)
    c: Horizontal(g3)
    c: PointOnObject(g3,g-2)
    c: DistanceY(g-1,g3) = 32.99
    c: DistanceY(g3,g0) = 2
    c: DistanceX(g3,g3) = 65
    c: DistanceX(g0,g0) = 65
    c: Coincident(g2,g1)
    c: Coincident(g4,g1)
    c: Coincident(g4,g1)
    c: PointOnObject(g2,g4)
    c: Coincident(g5,g2)
    c: Coincident(g5,g1)
    c: Vertical(g5)
    c: Angle(g4,g5) = 0.785398
    c: Coincident(g6,g2)
    c: Coincident(g6,g1)
    c: DistanceY(g-1,g1) = 11.75
    c: Horizontal(g7)
    c: Coincident(g7,g8)
    c: Coincident(g8,g9)
    c: Horizontal(g9)
    c: Angle(g7,g8) = 0.785398
    c: DistanceX(g7,g7) = 49
    c: Coincident(g9,g0)
    c: Coincident(g3,g7)
    c: PointOnObject(g0,g-2)
FEATURE [PartDesign::Pad] Pad003
  BaseFeature = -> Pocket015
  Direction = (1,1,1)
  Length = 15
  Length2 = 100
  Placement = pos=(0,0,0) rot=(1,0,0;1.5708rad)
  Profile = -> Sketch025
  Reversed = true
  Type = 0
FEATURE [Sketcher::SketchObject] Sketch026
  FullyConstrained = true
  MapMode = 5
  Placement = pos=(65,0,2.55e-14) rot=(0.707107,0,-0.707107;3.14159rad)
  Support = -> [DatumPlane002]
  sketch-geometry (3):
    g0: ArcOfCircle CenterX=-32 CenterY=3.5 CenterZ=0 NormalX=0 NormalY=0 NormalZ=1 AngleXU=0 Radius=1.60078 StartAngle=2.24554 EndAngle=4.03765
    g1: LineSegment StartX=-33 StartY=2.25 StartZ=0 EndX=-33 EndY=4.75 EndZ=0
    g2: LineSegment StartX=-11.75 StartY=0 StartZ=0 EndX=-11.75 EndY=10 EndZ=0
  constraints (11):
    c: Coincident(g1,g0)
    c: Coincident(g1,g0)
    c: Vertical(g1)
    c: DistanceX(g0,g-1) = 33
    c: DistanceX(g0,g0) = 1
    c: DistanceY(g0,g0) = 2.5
    c: DistanceY(g-1,g0) = 3.5
    c: Vertical(g2)
    c: DistanceY(g2,g2) = 10
    c: PointOnObject(g2,g-1)
    c: DistanceX(g2,g-1) = 11.75
FEATURE [PartDesign::Groove] Groove002
  Angle = 45
  Axis = (0,-1,2e-16)
  Base = (65,2.6e-15,11.75)
  BaseFeature = -> Pad003
  Placement = pos=(0,0,0) rot=(1,0,0;1.5708rad)
  Profile = -> Sketch026
  ReferenceAxis = -> Sketch026 [Edge3]
  Reversed = true
FEATURE [PartDesign::Pocket] Pocket016
  BaseFeature = -> Groove002
  Direction = (1,1,1)
  Length = 15
  Length2 = 100
  Placement = pos=(0,0,0) rot=(1,0,0;1.5708rad)
  Profile = -> Sketch026
  Reversed = true
  Type = 0
FEATURE [Sketcher::SketchObject] Sketch027
  FullyConstrained = true
  MapMode = 5
  Placement = pos=(0,-15,-2e-15) rot=(1,0,0;1.5708rad)
  Support = -> [DatumPlane003]
  sketch-geometry (4):
    g0: LineSegment StartX=-50 StartY=-5 StartZ=0 EndX=-39 EndY=-5 EndZ=0
    g1: LineSegment StartX=-39 StartY=-5 StartZ=0 EndX=-39 EndY=-15 EndZ=0
    g2: LineSegment StartX=-39 StartY=-15 StartZ=0 EndX=-50 EndY=-15 EndZ=0
    g3: LineSegment StartX=-50 StartY=-15 StartZ=0 EndX=-50 EndY=-5 EndZ=0
  constraints (12):
    c: Coincident(g0,g1)
    c: Coincident(g1,g2)
    c: Coincident(g2,g3)
    c: Coincident(g3,g0)
    c: Horizontal(g0)
    c: Horizontal(g2)
    c: Vertical(g1)
    c: Vertical(g3)
    c: DistanceX(g0,g0) = 11
    c: DistanceX(g0,g-1) = 39
    c: DistanceY(g0,g-1) = 5
    c: DistanceY(g3,g3) = 10
FEATURE [PartDesign::Pad] Pad004
  BaseFeature = -> Pocket016
  Direction = (1,1,1)
  Length = 1.4
  Length2 = 100
  Placement = pos=(0,0,0) rot=(1,0,0;1.5708rad)
  Profile = -> Sketch027
  Reversed = true
  Type = 0
FEATURE [Sketcher::SketchObject] Sketch028
  FullyConstrained = true
  MapMode = 5
  Placement = pos=(0,-15,-2e-15) rot=(1,0,0;1.5708rad)
  Support = -> [DatumPlane003]
  sketch-geometry (8):
    g0: LineSegment StartX=-50 StartY=-5 StartZ=0 EndX=-49 EndY=-5 EndZ=0
    g1: LineSegment StartX=-49 StartY=-5 StartZ=0 EndX=-49 EndY=-7 EndZ=0
    g2: LineSegment StartX=-49 StartY=-7 StartZ=0 EndX=-50 EndY=-7 EndZ=0
    g3: LineSegment StartX=-50 StartY=-7 StartZ=0 EndX=-50 EndY=-5 EndZ=0
    g4: LineSegment StartX=-50 StartY=-15 StartZ=0 EndX=-49 EndY=-15 EndZ=0
    g5: LineSegment StartX=-49 StartY=-15 StartZ=0 EndX=-49 EndY=-13 EndZ=0
    g6: LineSegment StartX=-49 StartY=-13 StartZ=0 EndX=-50 EndY=-13 EndZ=0
    g7: LineSegment StartX=-50 StartY=-13 StartZ=0 EndX=-50 EndY=-15 EndZ=0
  constraints (24):
    c: Coincident(g0,g1)
    c: Coincident(g1,g2)
    c: Coincident(g2,g3)
    c: Coincident(g3,g0)
    c: Horizontal(g0)
    c: Horizontal(g2)
    c: Vertical(g1)
    c: Vertical(g3)
    c: Coincident(g4,g5)
    c: Coincident(g5,g6)
    c: Coincident(g6,g7)
    c: Coincident(g7,g4)
    c: Horizontal(g4)
    c: Horizontal(g6)
    c: Vertical(g5)
    c: Vertical(g7)
    c: PointOnObject(g6,g3)
    c: PointOnObject(g5,g1)
    c: DistanceX(g2,g2) = 1
    c: DistanceY(g1,g1) = 2
    c: DistanceY(g5,g5) = 2
    c: DistanceY(g4,g0) = 10
    c: DistanceX(g0,g-1) = 50
    c: DistanceY(g0,g-1) = 5
FEATURE [PartDesign::Pad] Pad005
  BaseFeature = -> Pad004
  Direction = (1,1,1)
  Length = 13.4
  Length2 = 100
  Placement = pos=(0,0,0) rot=(1,0,0;1.5708rad)
  Profile = -> Sketch028
  Reversed = true
  Type = 0
FEATURE [Sketcher::SketchObject] Sketch029
  FullyConstrained = true
  MapMode = 5
  Placement = pos=(0,0,0) rot=(1,0,0;1.5708rad)
  Support = -> [XZ_Plane]
  sketch-geometry (13):
    g0: LineSegment StartX=-40 StartY=11.5 StartZ=0 EndX=-40 EndY=-3 EndZ=0
    g1: LineSegment StartX=-12 StartY=-5 StartZ=0 EndX=-20 EndY=-5 EndZ=0
    g2: LineSegment StartX=-20 StartY=-5 StartZ=0 EndX=-20 EndY=-3 EndZ=0
    g3: LineSegment StartX=-20 StartY=-3 StartZ=0 EndX=-40 EndY=-3 EndZ=0
    g4: LineSegment StartX=-40 StartY=11.5 StartZ=0 EndX=-37 EndY=11.5 EndZ=0
    g5: LineSegment StartX=-34.5 StartY=14 StartZ=0 EndX=-34.5 EndY=16 EndZ=0
    g6: LineSegment StartX=-34.5 StartY=16 StartZ=0 EndX=-8 EndY=16 EndZ=0
    g7: LineSegment StartX=-5.5 StartY=18.5 StartZ=0 EndX=0 EndY=18.5 EndZ=0
    g8: ArcOfCircle CenterX=-8 CenterY=18.5 CenterZ=0 NormalX=0 NormalY=0 NormalZ=1 AngleXU=0 Radius=2.5 StartAngle=4.71239 EndAngle=6.28319
    g9: ArcOfCircle CenterX=-37 CenterY=14 CenterZ=0 NormalX=0 NormalY=0 NormalZ=1 AngleXU=0 Radius=2.5 StartAngle=4.71239 EndAngle=6.28319
    g10: LineSegment StartX=0 StartY=18.5 StartZ=0 EndX=0 EndY=5.5 EndZ=0
    g11: LineSegment StartX=0 StartY=5.5 StartZ=0 EndX=-12 EndY=5.5 EndZ=0
    g12: LineSegment StartX=-12 StartY=5.5 StartZ=0 EndX=-12 EndY=-5 EndZ=0
  constraints (41):
    c: Vertical(g0)
    c: DistanceX(g0,g1) = 28
    c: DistanceY(g1,g7) = 23.5
    c: DistanceY(g1,g-1) = 5
    c: Horizontal(g1)
    c: Coincident(g1,g2)
    c: Vertical(g2)
    c: Coincident(g2,g3)
    c: Coincident(g3,g0)
    c: Horizontal(g3)
    c: DistanceX(g1,g1) = 8
    c: DistanceY(g2,g-1) = 3
    c: Horizontal(g4)
    c: Vertical(g5)
    c: Coincident(g5,g6)
    c: Horizontal(g6)
    c: Horizontal(g7)
    c: Coincident(g8,g6)
    c: Coincident(g8,g7)
    c: Tangent(g6,g8)
    c: Coincident(g9,g4)
    c: Coincident(g9,g5)
    c: Tangent(g9,g4)
    c: Tangent(g9,g5)
    c: DistanceX(g9,g-1) = 37
    c: DistanceX(g8,g-1) = 8
    c: DistanceY(g-1,g8) = 18.5
    c: DistanceY(g-1,g9) = 14
    c: Diameter(g8) = 5
    c: Diameter(g9) = 5
    c: PointOnObject(g7,g-2)
    c: Coincident(g7,g10)
    c: Vertical(g10)
    c: Coincident(g10,g11)
    c: Horizontal(g11)
    c: Coincident(g11,g12)
    c: Coincident(g12,g1)
    c: Vertical(g12)
    c: DistanceY(g10,g10) = 13
    c: DistanceX(g1,g-1) = 12
    c: Coincident(g0,g4)
FEATURE [PartDesign::Pocket] Pocket017  label="upper-electronics-cutout"
  BaseFeature = -> Pad005
  Direction = (1,1,1)
  Length = 5.5
  Length2 = 100
  Placement = pos=(0,0,0) rot=(1,0,0;1.5708rad)
  Profile = -> Sketch029
  Reversed = true
  Type = 0
FEATURE [Sketcher::SketchObject] Sketch030
  FullyConstrained = true
  MapMode = 5
  Placement = pos=(0,0,0) rot=(1,0,0;1.5708rad)
  Support = -> [XZ_Plane]
  sketch-geometry (6):
    g0: LineSegment StartX=-23 StartY=-38 StartZ=0 EndX=-39 EndY=-38 EndZ=0
    g1: LineSegment StartX=-39 StartY=-38 StartZ=0 EndX=-39 EndY=-17 EndZ=0
    g2: LineSegment StartX=-39 StartY=-17 StartZ=0 EndX=0 EndY=-17 EndZ=0
    g3: LineSegment StartX=-23 StartY=-40 StartZ=0 EndX=-23 EndY=-38 EndZ=0
    g4: LineSegment StartX=0 StartY=-17 StartZ=0 EndX=0 EndY=-40 EndZ=0
    g5: LineSegment StartX=0 StartY=-40 StartZ=0 EndX=-23 EndY=-40 EndZ=0
  constraints (18):
    c: Coincident(g0,g1)
    c: Coincident(g1,g2)
    c: Horizontal(g0)
    c: Horizontal(g2)
    c: Vertical(g1)
    c: DistanceY(g0,g-1) = 38
    c: DistanceY(g2,g-1) = 17
    c: Coincident(g0,g3)
    c: Vertical(g3)
    c: PointOnObject(g2,g-2)
    c: Coincident(g2,g4)
    c: Vertical(g4)
    c: Coincident(g4,g5)
    c: Horizontal(g5)
    c: Coincident(g3,g5)
    c: DistanceX(g3,g-1) = 23
    c: DistanceY(g3,g3) = 2
    c: DistanceX(g1,g-1) = 39
FEATURE [PartDesign::Pocket] Pocket018  label="lower-electronics-cutout"
  BaseFeature = -> Pocket017
  Direction = (1,1,1)
  Length = 12.5
  Length2 = 100
  Placement = pos=(0,0,0) rot=(1,0,0;1.5708rad)
  Profile = -> Sketch030
  Reversed = true
  Type = 0
FEATURE [Sketcher::SketchObject] Sketch031
  FullyConstrained = true
  MapMode = 5
  Placement = pos=(0,-15,-2e-15) rot=(1,0,0;1.5708rad)
  Support = -> [DatumPlane003]
  sketch-geometry (21):
    g0: LineSegment StartX=-42.9123 StartY=-36.75 StartZ=0 EndX=-41.3246 EndY=-34 EndZ=0
    g1: LineSegment StartX=-41.3246 StartY=-34 StartZ=0 EndX=-42.9123 EndY=-31.25 EndZ=0
    g2: LineSegment StartX=-42.9123 StartY=-31.25 StartZ=0 EndX=-46.0877 EndY=-31.25 EndZ=0
    g3: LineSegment StartX=-46.0877 StartY=-31.25 StartZ=0 EndX=-47.6754 EndY=-34 EndZ=0
    g4: LineSegment StartX=-47.6754 StartY=-34 StartZ=0 EndX=-46.0877 EndY=-36.75 EndZ=0
    g5: LineSegment StartX=-46.0877 StartY=-36.75 StartZ=0 EndX=-42.9123 EndY=-36.75 EndZ=0
    g6: Circle CenterX=-44.5 CenterY=-34 CenterZ=0 NormalX=0 NormalY=0 NormalZ=1 AngleXU=0 Radius=3.17543
    g7: LineSegment StartX=-34.25 StartY=12.4123 StartZ=0 EndX=-34.25 EndY=15.5877 EndZ=0
    g8: LineSegment StartX=-34.25 StartY=15.5877 StartZ=0 EndX=-37 EndY=17.1754 EndZ=0
    g9: LineSegment StartX=-37 StartY=17.1754 StartZ=0 EndX=-39.75 EndY=15.5877 EndZ=0
    g10: LineSegment StartX=-39.75 StartY=15.5877 StartZ=0 EndX=-39.75 EndY=12.4123 EndZ=0
    g11: LineSegment StartX=-39.75 StartY=12.4123 StartZ=0 EndX=-37 EndY=10.8246 EndZ=0
    g12: LineSegment StartX=-37 StartY=10.8246 StartZ=0 EndX=-34.25 EndY=12.4123 EndZ=0
    g13: Circle CenterX=-37 CenterY=14 CenterZ=0 NormalX=0 NormalY=0 NormalZ=1 AngleXU=0 Radius=3.17543
    g14: LineSegment StartX=-5.25 StartY=16.9123 StartZ=0 EndX=-5.25 EndY=20.0877 EndZ=0
    g15: LineSegment StartX=-5.25 StartY=20.0877 StartZ=0 EndX=-8 EndY=21.6754 EndZ=0
    g16: LineSegment StartX=-8 StartY=21.6754 StartZ=0 EndX=-10.75 EndY=20.0877 EndZ=0
    g17: LineSegment StartX=-10.75 StartY=20.0877 StartZ=0 EndX=-10.75 EndY=16.9123 EndZ=0
    g18: LineSegment StartX=-10.75 StartY=16.9123 StartZ=0 EndX=-8 EndY=15.3246 EndZ=0
    g19: LineSegment StartX=-8 StartY=15.3246 StartZ=0 EndX=-5.25 EndY=16.9123 EndZ=0
    g20: Circle CenterX=-8 CenterY=18.5 CenterZ=0 NormalX=0 NormalY=0 NormalZ=1 AngleXU=0 Radius=3.17543
  constraints (51):
    c: Coincident(g0,g1)
    c: Coincident(g1,g2)
    c: Coincident(g2,g3)
    c: Coincident(g3,g4)
    c: Coincident(g4,g5)
    c: Coincident(g5,g0)
    c: Equal(g0, g1-g5) x5
    c: PointOnObject(g0,g6)
    c: PointOnObject(g1,g6)
    c: PointOnObject(g2,g6)
    c: PointOnObject(g3,g6)
    c: PointOnObject(g4,g6)
    c: PointOnObject(g5,g6)
    c: DistanceY(g4,g2) = 5.5
    c: Horizontal(g5)
    c: Coincident(g7,g8)
    c: Coincident(g8,g9)
    c: Coincident(g9,g10)
    c: Coincident(g10,g11)
    c: Coincident(g11,g12)
    c: Coincident(g12,g7)
    c: Equal(g7, g8-g12) x5
    c: PointOnObject(g7,g13)
    c: PointOnObject(g8,g13)
    c: PointOnObject(g9,g13)
    c: PointOnObject(g10,g13)
    c: PointOnObject(g11,g13)
    c: PointOnObject(g12,g13)
    c: Coincident(g14,g15)
    c: Coincident(g15,g16)
    c: Coincident(g16,g17)
    c: Coincident(g17,g18)
    c: Coincident(g18,g19)
    c: Coincident(g19,g14)
    c: Equal(g14, g15-g19) x5
    c: PointOnObject(g14,g20)
    c: PointOnObject(g15,g20)
    c: PointOnObject(g16,g20)
    c: PointOnObject(g17,g20)
    c: PointOnObject(g18,g20)
    c: PointOnObject(g19,g20)
    c: DistanceX(g16,g14) = 5.5
    c: Vertical(g17)
    c: Vertical(g10)
    c: DistanceX(g10,g7) = 5.5
    c: DistanceY(g6,g-1) = 34
    c: DistanceX(g6,g-1) = 44.5
    c: DistanceX(g13,g-1) = 37
    c: DistanceX(g20,g-1) = 8
    c: DistanceY(g-1,g13) = 14
    c: DistanceY(g-1,g20) = 18.5
FEATURE [PartDesign::Pocket] Pocket019
  BaseFeature = -> Pocket018
  Direction = (1,1,1)
  Length = 2.5
  Length2 = 100
  Placement = pos=(0,0,0) rot=(1,0,0;1.5708rad)
  Profile = -> Sketch031
  Type = 0
FEATURE [Sketcher::SketchObject] Sketch032
  FullyConstrained = true
  MapMode = 5
  Placement = pos=(0,0,0) rot=(1,0,0;1.5708rad)
  Support = -> [XZ_Plane]
  sketch-geometry (3):
    g0: Circle CenterX=-20 CenterY=-28.5 CenterZ=0 NormalX=0 NormalY=0 NormalZ=1 AngleXU=0 Radius=1.6
    g1: Circle CenterX=-20 CenterY=-34.5 CenterZ=0 NormalX=0 NormalY=0 NormalZ=1 AngleXU=0 Radius=1.6
    g2: LineSegment StartX=-20 StartY=-28.5 StartZ=0 EndX=-20 EndY=-34.5 EndZ=0
  constraints (8):
    c: Diameter(g0) = 3.2
    c: Diameter(g1) = 3.2
    c: Coincident(g2,g0)
    c: Coincident(g2,g1)
    c: Vertical(g2)
    c: DistanceY(g2,g2) = 6
    c: DistanceX(g0,g-1) = 20
    c: DistanceY(g0,g-1) = 28.5
FEATURE [PartDesign::Pocket] Pocket020
  BaseFeature = -> Pocket019
  Direction = (1,1,1)
  Length = 21
  Length2 = 100
  Placement = pos=(0,0,0) rot=(1,0,0;1.5708rad)
  Profile = -> Sketch032
  Reversed = true
  Type = 0
FEATURE [Sketcher::SketchObject] Sketch033
  FullyConstrained = false
  MapMode = 5
  Placement = pos=(0,0,0) rot=(1,0,0;1.5708rad)
  Support = -> [XZ_Plane]
  sketch-geometry (4):
    g0: LineSegment StartX=0 StartY=33 StartZ=0 EndX=55.0377 EndY=33 EndZ=0
    g1: LineSegment StartX=0 StartY=33 StartZ=0 EndX=0 EndY=24 EndZ=0
    g2: LineSegment StartX=0 StartY=24 StartZ=0 EndX=55.0377 EndY=24 EndZ=0
    g3: LineSegment StartX=55.0377 StartY=33 StartZ=0 EndX=55.0377 EndY=24 EndZ=0
  constraints (11):
    c: PointOnObject(g0,g-2)
    c: Horizontal(g0)
    c: Coincident(g1,g0)
    c: PointOnObject(g1,g-2)
    c: Coincident(g2,g1)
    c: Horizontal(g2)
    c: DistanceY(g-1,g0) = 33
    c: DistanceY(g-1,g1) = 24
    c: Coincident(g3,g0)
    c: Coincident(g3,g2)
    c: Vertical(g3)
FEATURE [PartDesign::Pocket] Pocket021
  BaseFeature = -> Pocket020
  Direction = (1,1,1)
  Length = 4.1
  Length2 = 100
  Placement = pos=(0,0,0) rot=(1,0,0;1.5708rad)
  Profile = -> Sketch033
  Reversed = true
  Type = 0
FEATURE [Sketcher::SketchObject] Sketch034
  FullyConstrained = true
  MapMode = 5
  Placement = pos=(0,0,0) rot=(1,0,0;1.5708rad)
  Support = -> [XZ_Plane]
  sketch-geometry (2):
    g0: Circle CenterX=55 CenterY=-15 CenterZ=0 NormalX=0 NormalY=0 NormalZ=1 AngleXU=0 Radius=1.6
    g1: Circle CenterX=10 CenterY=20 CenterZ=0 NormalX=0 NormalY=0 NormalZ=1 AngleXU=0 Radius=1.6
  constraints (6):
    c: Diameter(g1) = 3.2
    c: Diameter(g0) = 3.2
    c: DistanceX(g-1,g1) = 10
    c: DistanceY(g-1,g1) = 20
    c: DistanceY(g0,g-1) = 15
    c: DistanceX(g-1,g0) = 55
FEATURE [PartDesign::Pocket] Pocket022
  BaseFeature = -> Pocket021
  Direction = (1,1,1)
  Length = 15
  Length2 = 100
  Placement = pos=(0,0,0) rot=(1,0,0;1.5708rad)
  Profile = -> Sketch034
  Reversed = true
  Type = 0
FEATURE [Sketcher::SketchObject] Sketch035
  FullyConstrained = true
  MapMode = 5
  Placement = pos=(0,-15,-2e-15) rot=(1,0,0;1.5708rad)
  Support = -> [DatumPlane003]
  sketch-geometry (14):
    g0: LineSegment StartX=12.75 StartY=18.4123 StartZ=0 EndX=12.75 EndY=21.5877 EndZ=0
    g1: LineSegment StartX=12.75 StartY=21.5877 StartZ=0 EndX=10 EndY=23.1754 EndZ=0
    g2: LineSegment StartX=10 StartY=23.1754 StartZ=0 EndX=7.25 EndY=21.5877 EndZ=0
    g3: LineSegment StartX=7.25 StartY=21.5877 StartZ=0 EndX=7.25 EndY=18.4123 EndZ=0
    g4: LineSegment StartX=7.25 StartY=18.4123 StartZ=0 EndX=10 EndY=16.8246 EndZ=0
    g5: LineSegment StartX=10 StartY=16.8246 StartZ=0 EndX=12.75 EndY=18.4123 EndZ=0
    g6: Circle CenterX=10 CenterY=20 CenterZ=0 NormalX=0 NormalY=0 NormalZ=1 AngleXU=0 Radius=3.17543
    g7: LineSegment StartX=57.75 StartY=-16.5877 StartZ=0 EndX=57.75 EndY=-13.4123 EndZ=0
    g8: LineSegment StartX=57.75 StartY=-13.4123 StartZ=0 EndX=55 EndY=-11.8246 EndZ=0
    g9: LineSegment StartX=55 StartY=-11.8246 StartZ=0 EndX=52.25 EndY=-13.4123 EndZ=0
    g10: LineSegment StartX=52.25 StartY=-13.4123 StartZ=0 EndX=52.25 EndY=-16.5877 EndZ=0
    g11: LineSegment StartX=52.25 StartY=-16.5877 StartZ=0 EndX=55 EndY=-18.1754 EndZ=0
    g12: LineSegment StartX=55 StartY=-18.1754 StartZ=0 EndX=57.75 EndY=-16.5877 EndZ=0
    g13: Circle CenterX=55 CenterY=-15 CenterZ=0 NormalX=0 NormalY=0 NormalZ=1 AngleXU=0 Radius=3.17543
  constraints (34):
    c: Coincident(g0,g1)
    c: Coincident(g1,g2)
    c: Coincident(g2,g3)
    c: Coincident(g3,g4)
    c: Coincident(g4,g5)
    c: Coincident(g5,g0)
    c: Equal(g0, g1-g5) x5
    c: PointOnObject(g0,g6)
    c: PointOnObject(g1,g6)
    c: PointOnObject(g2,g6)
    c: PointOnObject(g3,g6)
    c: PointOnObject(g4,g6)
    c: PointOnObject(g5,g6)
    c: Coincident(g7,g8)
    c: Coincident(g8,g9)
    c: Coincident(g9,g10)
    c: Coincident(g10,g11)
    c: Coincident(g11,g12)
    c: Coincident(g12,g7)
    c: Equal(g7, g8-g12) x5
    c: PointOnObject(g7,g13)
    c: PointOnObject(g8,g13)
    c: PointOnObject(g9,g13)
    c: PointOnObject(g10,g13)
    c: PointOnObject(g11,g13)
    c: PointOnObject(g12,g13)
    c: Vertical(g10)
    c: Vertical(g3)
    c: DistanceX(g2,g0) = 5.5
    c: DistanceX(g9,g7) = 5.5
    c: DistanceX(g-1,g6) = 10
    c: DistanceY(g-1,g6) = 20
    c: DistanceY(g13,g-1) = 15
    c: DistanceX(g-1,g13) = 55
FEATURE [PartDesign::Pocket] Pocket023
  BaseFeature = -> Pocket022
  Direction = (1,1,1)
  Length = 2.5
  Length2 = 100
  Placement = pos=(0,0,0) rot=(1,0,0;1.5708rad)
  Profile = -> Sketch035
  Type = 0
FEATURE [Sketcher::SketchObject] Sketch036
  FullyConstrained = true
  MapMode = 5
  Placement = pos=(0,-15,-2e-15) rot=(1,0,0;1.5708rad)
  Support = -> [DatumPlane003]
  sketch-geometry (3):
    g0: Circle CenterX=-20 CenterY=-28.5 CenterZ=0 NormalX=0 NormalY=0 NormalZ=1 AngleXU=0 Radius=2.95
    g1: Circle CenterX=-20 CenterY=-34.5 CenterZ=0 NormalX=0 NormalY=0 NormalZ=1 AngleXU=0 Radius=2.95
    g2: LineSegment StartX=-20 StartY=-28.5 StartZ=0 EndX=-20 EndY=-34.5 EndZ=0
  constraints (8):
    c: Diameter(g0) = 5.9
    c: Diameter(g1) = 5.9
    c: Coincident(g2,g0)
    c: Coincident(g2,g1)
    c: Vertical(g2)
    c: DistanceY(g2,g2) = 6
    c: DistanceY(g0,g-1) = 28.5
    c: DistanceX(g0,g-1) = 20
FEATURE [PartDesign::Pocket] Pocket024
  BaseFeature = -> Pocket023
  Direction = (1,1,1)
  Length = 1.75
  Length2 = 100
  Placement = pos=(0,0,0) rot=(1,0,0;1.5708rad)
  Profile = -> Sketch036
  Type = 0
FEATURE [PartDesign::Chamfer] Chamfer001
  Angle = 45
  Base = -> Pocket024 [Edge473,Edge475]
  BaseFeature = -> Pocket024
  ChamferType = 0
  FlipDirection = false
  Placement = pos=(0,0,0) rot=(1,0,0;1.5708rad)
  Size = 1.2
  Size2 = 1.1
  SupportTransform = false
  UseAllEdges = false
FEATURE [Sketcher::SketchObject] Sketch037
  FullyConstrained = false
  MapMode = 5
  Placement = pos=(0,0,0) rot=(1,0,0;1.5708rad)
  Support = -> [XZ_Plane]
  sketch-geometry (4):
    g0: LineSegment StartX=-0.755086 StartY=14.6906 StartZ=0 EndX=29.6374 EndY=14.6906 EndZ=0
    g1: LineSegment StartX=29.6374 StartY=14.6906 StartZ=0 EndX=29.6374 EndY=6.59491 EndZ=0
    g2: LineSegment StartX=29.6374 StartY=6.59491 StartZ=0 EndX=-0.755086 EndY=6.59491 EndZ=0
    g3: LineSegment StartX=-0.755086 StartY=6.59491 StartZ=0 EndX=-0.755086 EndY=14.6906 EndZ=0
  constraints (8):
    c: Coincident(g0,g1)
    c: Coincident(g1,g2)
    c: Coincident(g2,g3)
    c: Coincident(g3,g0)
    c: Horizontal(g0)
    c: Horizontal(g2)
    c: Vertical(g1)
    c: Vertical(g3)
FEATURE [PartDesign::Pocket] Pocket025
  BaseFeature = -> Chamfer001
  Direction = (1,1,1)
  Length = 4.6
  Length2 = 100
  Placement = pos=(0,0,0) rot=(1,0,0;1.5708rad)
  Profile = -> Sketch037
  Reversed = true
  Type = 0
FEATURE [PartDesign::Plane] DatumPlane005
  AttachmentOffset = pos=(0,0,0) rot=(0,0,1;3.14159rad)
  Length = 158.62
  MapMode = 5
  Placement = pos=(0,-13.6,-3e-15) rot=(0,0.707107,0.707107;3.14159rad)
  ResizeMode = 0
  Support = -> [Pocket025]
  Width = 110.938
FEATURE [Sketcher::SketchObject] Sketch038
  FullyConstrained = true
  MapMode = 5
  Placement = pos=(0,-13.6,-3e-15) rot=(0,0.707107,0.707107;3.14159rad)
  Support = -> [DatumPlane005]
  sketch-geometry (4):
    g0: LineSegment StartX=12 StartY=-5 StartZ=0 EndX=18 EndY=-5 EndZ=0
    g1: LineSegment StartX=18 StartY=-5 StartZ=0 EndX=18 EndY=-9.5 EndZ=0
    g2: LineSegment StartX=18 StartY=-9.5 StartZ=0 EndX=12 EndY=-9.5 EndZ=0
    g3: LineSegment StartX=12 StartY=-9.5 StartZ=0 EndX=12 EndY=-5 EndZ=0
  constraints (12):
    c: Coincident(g0,g1)
    c: Coincident(g1,g2)
    c: Coincident(g2,g3)
    c: Coincident(g3,g0)
    c: Horizontal(g0)
    c: Horizontal(g2)
    c: Vertical(g1)
    c: Vertical(g3)
    c: DistanceX(g0,g0) = 6
    c: DistanceY(g1,g1) = 4.5
    c: DistanceX(g-1,g2) = 12
    c: DistanceY(g0,g-1) = 5
FEATURE [PartDesign::Pad] Pad006
  BaseFeature = -> Pocket025
  Direction = (1,1,1)
  Length = 8.1
  Length2 = 100
  Placement = pos=(0,0,0) rot=(1,0,0;1.5708rad)
  Profile = -> Sketch038
  Type = 0
FEATURE [PartDesign::Plane] DatumPlane006
  Length = 153.11
  MapMode = 5
  Placement = pos=(0,-1.15e-14,34.99) rot=(0,0,1;3.14159rad)
  ResizeMode = 0
  Support = -> [Pad006]
  Width = 66.5277
FEATURE [Sketcher::SketchObject] Sketch039
  FullyConstrained = true
  MapMode = 5
  Placement = pos=(0,-1.15e-14,34.99) rot=(0,0,1;3.14159rad)
  Support = -> [DatumPlane006]
  sketch-geometry (4):
    g0: LineSegment StartX=-64 StartY=2.25 StartZ=0 EndX=-50 EndY=2.25 EndZ=0
    g1: LineSegment StartX=-51.5 StartY=9 StartZ=0 EndX=-64 EndY=9 EndZ=0
    g2: LineSegment StartX=-64 StartY=9 StartZ=0 EndX=-64 EndY=2.25 EndZ=0
    g3: LineSegment StartX=-50 StartY=2.25 StartZ=0 EndX=-51.5 EndY=9 EndZ=0
  constraints (12):
    c: Coincident(g1,g2)
    c: Coincident(g2,g0)
    c: Horizontal(g0)
    c: Horizontal(g1)
    c: Vertical(g2)
    c: DistanceY(g2,g2) = 6.75
    c: DistanceX(g1,g1) = 12.5
    c: DistanceX(g0,g-1) = 50
    c: DistanceY(g-1,g0) = 2.25
    c: DistanceX(g0,g0) = 14
    c: Coincident(g3,g0)
    c: Coincident(g3,g1)
FEATURE [PartDesign::Pocket] Pocket026
  BaseFeature = -> Pad006
  Direction = (1,1,1)
  Length = 3
  Length2 = 100
  Placement = pos=(0,0,0) rot=(1,0,0;1.5708rad)
  Profile = -> Sketch039
  Type = 0
FEATURE [Sketcher::SketchObject] Sketch040
  FullyConstrained = true
  MapMode = 5
  Placement = pos=(0,-15,-2e-15) rot=(1,0,0;1.5708rad)
  Support = -> [DatumPlane003]
  sketch-geometry (7):
    g0: LineSegment StartX=-11.5 StartY=4 StartZ=0 EndX=-4 EndY=4 EndZ=0
    g1: LineSegment StartX=-4 StartY=4 StartZ=0 EndX=-4 EndY=-17 EndZ=0
    g2: LineSegment StartX=-4 StartY=-17 StartZ=0 EndX=0 EndY=-17 EndZ=0
    g3: LineSegment StartX=0 StartY=-17 StartZ=0 EndX=0 EndY=-40 EndZ=0
    g4: LineSegment StartX=0 StartY=-40 StartZ=0 EndX=-33 EndY=-40 EndZ=0
    g5: LineSegment StartX=-33 StartY=-40 StartZ=0 EndX=-20.5 EndY=-29 EndZ=0
    g6: LineSegment StartX=-20.5 StartY=-29 StartZ=0 EndX=-11.5 EndY=4 EndZ=0
  constraints (21):
    c: Horizontal(g0)
    c: Coincident(g0,g1)
    c: Vertical(g1)
    c: Horizontal(g2)
    c: Coincident(g2,g3)
    c: Vertical(g3)
    c: Coincident(g3,g4)
    c: Horizontal(g4)
    c: DistanceX(g0,g0) = 7.5
    c: DistanceX(g0,g-1) = 4
    c: DistanceY(g2,g-1) = 17
    c: PointOnObject(g2,g-2)
    c: DistanceY(g3,g-1) = 40
    c: DistanceY(g-1,g0) = 4
    c: Coincident(g1,g2)
    c: Coincident(g6,g5)
    c: Coincident(g6,g0)
    c: DistanceX(g5,g-1) = 20.5
    c: DistanceY(g5,g-1) = 29
    c: Coincident(g4,g5)
    c: DistanceX(g4,g4) = 33
FEATURE [PartDesign::Pocket] Pocket027
  BaseFeature = -> Pocket026
  Direction = (1,1,1)
  Length = 8
  Length2 = 100
  Placement = pos=(0,0,0) rot=(1,0,0;1.5708rad)
  Profile = -> Sketch040
  Type = 0
FEATURE [Sketcher::SketchObject] Sketch041
  FullyConstrained = false
  MapMode = 5
  Placement = pos=(0,0,0) rot=(1,0,0;1.5708rad)
  Support = -> [XZ_Plane]
  sketch-geometry (6):
    g0: LineSegment StartX=20.25 StartY=0 StartZ=0 EndX=25.25 EndY=0 EndZ=0
    g1: LineSegment StartX=25.25 StartY=0 StartZ=0 EndX=25.25 EndY=-7 EndZ=0
    g2: LineSegment StartX=20.25 StartY=0 StartZ=0 EndX=13.407 EndY=-4.71528 EndZ=0
    g3: LineSegment StartX=13.407 StartY=-4.71528 StartZ=0 EndX=13.407 EndY=-25.2934 EndZ=0
    g4: LineSegment StartX=25.25 StartY=-7 StartZ=0 EndX=43.5434 EndY=-25.2934 EndZ=0
    g5: LineSegment StartX=43.5434 StartY=-25.2934 StartZ=0 EndX=13.407 EndY=-25.2934 EndZ=0
  constraints (15):
    c: Coincident(g0,g1)
    c: Horizontal(g0)
    c: Vertical(g1)
    c: PointOnObject(g0,g-1)
    c: DistanceX(g-1,g0) = 20.25
    c: Coincident(g0,g2)
    c: Coincident(g2,g3)
    c: Vertical(g3)
    c: Coincident(g4,g1)
    c: Coincident(g5,g4)
    c: Coincident(g5,g3)
    c: Horizontal(g5)
    c: DistanceX(g-1,g1) = 25.25
    c: DistanceY(g1,g-1) = 7
    c: Angle(g4,g1) = 2.35619
FEATURE [PartDesign::Pocket] Pocket028
  BaseFeature = -> Pocket027
  Direction = (1,1,1)
  Length = 6.6
  Length2 = 100
  Placement = pos=(0,0,0) rot=(1,0,0;1.5708rad)
  Profile = -> Sketch041
  Reversed = true
  Type = 0
FEATURE [Sketcher::SketchObject] Sketch042
  FullyConstrained = true
  MapMode = 5
  Placement = pos=(0,-15,-2e-15) rot=(1,0,0;1.5708rad)
  Support = -> [DatumPlane003]
  sketch-geometry (3):
    g0: LineSegment StartX=-33 StartY=-40 StartZ=0 EndX=-20.5 EndY=-29 EndZ=0
    g1: LineSegment StartX=-20.5 StartY=-29 StartZ=0 EndX=-20.5 EndY=-40 EndZ=0
    g2: LineSegment StartX=-20.5 StartY=-40 StartZ=0 EndX=-33 EndY=-40 EndZ=0
  constraints (9):
    c: Coincident(g0,g1)
    c: Vertical(g1)
    c: Coincident(g1,g2)
    c: Coincident(g2,g0)
    c: Horizontal(g2)
    c: DistanceX(g1,g-1) = 20.5
    c: DistanceX(g0,g-1) = 33
    c: DistanceY(g1,g-1) = 40
    c: DistanceY(g0,g-1) = 29
FEATURE [PartDesign::Pocket] Pocket029
  BaseFeature = -> Pocket028
  Direction = (1,1,1)
  Length = 5
  Length2 = 100
  Placement = pos=(0,0,0) rot=(1,0,0;1.5708rad)
  Profile = -> Sketch042
  Type = 1
FEATURE [Sketcher::SketchObject] Sketch043
  FullyConstrained = true
  MapMode = 5
  Placement = pos=(0,-15,-2e-15) rot=(1,0,0;1.5708rad)
  Support = -> [DatumPlane003]
  sketch-geometry (9):
    g0: LineSegment StartX=-33 StartY=-40 StartZ=0 EndX=-37.5411 EndY=-40 EndZ=0
    g1: LineSegment StartX=-37.5411 StartY=-40 StartZ=0 EndX=-23.1575 EndY=-27.3424 EndZ=0
    g2: LineSegment StartX=-23.1575 StartY=-27.3424 StartZ=0 EndX=-20.3368 EndY=-17 EndZ=0
    g3: LineSegment StartX=-20.3368 StartY=-17 StartZ=0 EndX=-17.2273 EndY=-17 EndZ=0
    g4: LineSegment StartX=-17.2273 StartY=-17 StartZ=0 EndX=-20.5 EndY=-29 EndZ=0
    g5: LineSegment StartX=-20.5 StartY=-29 StartZ=0 EndX=-33 EndY=-40 EndZ=0
    g6: LineSegment StartX=-17.2273 StartY=-17 StartZ=0 EndX=-11.5 EndY=4 EndZ=0
    g7: LineSegment StartX=-23.1575 StartY=-27.3424 StartZ=0 EndX=-20.2632 EndY=-28.1318 EndZ=0
    g8: LineSegment StartX=-23.1575 StartY=-27.3424 StartZ=0 EndX=-21.1756 EndY=-29.5945 EndZ=0
  constraints (27):
    c: Horizontal(g0)
    c: Coincident(g0,g1)
    c: Coincident(g1,g2)
    c: Coincident(g2,g3)
    c: Horizontal(g3)
    c: Coincident(g3,g4)
    c: Coincident(g4,g5)
    c: Coincident(g5,g0)
    c: DistanceX(g4,g-1) = 20.5
    c: Coincident(g6,g3)
    c: Parallel(g6,g4)
    c: DistanceX(g6,g-1) = 11.5
    c: DistanceY(g-1,g6) = 4
    c: DistanceY(g3,g-1) = 17
    c: DistanceY(g0,g-1) = 40
    c: DistanceX(g0,g-1) = 33
    c: Coincident(g7,g1)
    c: PointOnObject(g7,g4)
    c: Coincident(g8,g1)
    c: PointOnObject(g8,g5)
    c: Perpendicular(g4,g7)
    c: Perpendicular(g5,g8)
    c: Distance(g7) = 3
    c: Distance(g8) = 3
    c: DistanceY(g4,g-1) = 29
    c: Parallel(g1,g5)
    c: Parallel(g2,g4)
FEATURE [PartDesign::Pad] Pad007
  BaseFeature = -> Pocket029
  Direction = (1,1,1)
  Length = 10
  Length2 = 100
  Placement = pos=(0,0,0) rot=(1,0,0;1.5708rad)
  Profile = -> Sketch043
  Reversed = true
  Type = 0
FEATURE [Sketcher::SketchObject] Sketch044
  FullyConstrained = false
  MapMode = 5
  Placement = pos=(0,0,0) rot=(1,0,0;1.5708rad)
  Support = -> [XZ_Plane]
  sketch-geometry (8):
    g0: LineSegment StartX=-60.478 StartY=-50.0111 StartZ=0 EndX=-18.9502 EndY=-50.0111 EndZ=0
    g1: LineSegment StartX=-18.9502 StartY=-50.0111 StartZ=0 EndX=-18.9502 EndY=11.5695 EndZ=0
    g2: LineSegment StartX=-18.9502 StartY=11.5695 StartZ=0 EndX=34.3817 EndY=11.5695 EndZ=0
    g3: LineSegment StartX=34.3817 StartY=11.5695 StartZ=0 EndX=34.3817 EndY=-29.8161 EndZ=0
    g4: LineSegment StartX=34.3817 StartY=-29.8161 StartZ=0 EndX=94.3979 EndY=-29.8161 EndZ=0
    g5: LineSegment StartX=94.3979 StartY=-29.8161 StartZ=0 EndX=94.3979 EndY=43.8531 EndZ=0
    g6: LineSegment StartX=94.3979 StartY=43.8531 StartZ=0 EndX=-60.478 EndY=43.8531 EndZ=0
    g7: LineSegment StartX=-60.478 StartY=43.8531 StartZ=0 EndX=-60.478 EndY=-50.0111 EndZ=0
  constraints (16):
    c: Horizontal(g0)
    c: Coincident(g0,g1)
    c: Vertical(g1)
    c: Coincident(g1,g2)
    c: Horizontal(g2)
    c: Coincident(g2,g3)
    c: Coincident(g3,g4)
    c: Horizontal(g4)
    c: Coincident(g4,g5)
    c: Coincident(g5,g6)
    c: Horizontal(g6)
    c: Coincident(g6,g7)
    c: Coincident(g7,g0)
    c: Vertical(g7)
    c: Vertical(g5)
    c: Vertical(g3)
FEATURE [PartDesign::Plane] DatumPlane007
  Length = 72.475
  MapMode = 5
  Placement = pos=(-11.7192,0,3.19615) rot=(0.794707,0,0.606994;3.14159rad)
  ResizeMode = 0
  Width = 61.081
FEATURE [Sketcher::SketchObject] Sketch045
  FullyConstrained = true
  MapMode = 5
  Placement = pos=(-11.7192,0,3.19615) rot=(0.794707,0,0.606994;3.14159rad)
  Support = -> [DatumPlane007]
  sketch-geometry (1):
    g0: Circle CenterX=-24.5 CenterY=11 CenterZ=0 NormalX=0 NormalY=0 NormalZ=1 AngleXU=0 Radius=3.5
  constraints (3):
    c: DistanceX(g0,g-1) = 24.5
    c: DistanceY(g-1,g0) = 11
    c: Diameter(g0) = 7
FEATURE [PartDesign::Pocket] Pocket031
  BaseFeature = -> Pad007
  Direction = (1,1,1)
  Length = 2
  Length2 = 100
  Placement = pos=(0,0,0) rot=(1,0,0;1.5708rad)
  Profile = -> Sketch045
  Type = 0
FEATURE [Sketcher::SketchObject] Sketch046
  FullyConstrained = false
  MapMode = 5
  Placement = pos=(0,-13.6,-3e-15) rot=(0,0.707107,0.707107;3.14159rad)
  Support = -> [DatumPlane005]
  sketch-geometry (4):
    g0: LineSegment StartX=45.9588 StartY=-27.9578 StartZ=0 EndX=39.2523 EndY=-27.9578 EndZ=0
    g1: LineSegment StartX=39.2523 StartY=-27.9578 StartZ=0 EndX=39.2523 EndY=-16.0357 EndZ=0
    g2: LineSegment StartX=39.2523 StartY=-16.0357 StartZ=0 EndX=45.9588 EndY=-16.0357 EndZ=0
    g3: LineSegment StartX=45.9588 StartY=-16.0357 StartZ=0 EndX=45.9588 EndY=-27.9578 EndZ=0
  constraints (8):
    c: Coincident(g0,g1)
    c: Coincident(g1,g2)
    c: Coincident(g2,g3)
    c: Coincident(g3,g0)
    c: Horizontal(g0)
    c: Horizontal(g2)
    c: Vertical(g1)
    c: Vertical(g3)
FEATURE [PartDesign::Pad] Pad008
  BaseFeature = -> Pocket031
  Direction = (1,1,1)
  Length = 4
  Length2 = 100
  Placement = pos=(0,0,0) rot=(1,0,0;1.5708rad)
  Profile = -> Sketch046
  Type = 0
FEATURE [Sketcher::SketchObject] Sketch047
  FullyConstrained = true
  MapMode = 5
  Placement = pos=(0,-13.6,-3e-15) rot=(0,0.707107,0.707107;3.14159rad)
  Support = -> [DatumPlane005]
  sketch-geometry (1):
    g0: Circle CenterX=44.5 CenterY=-22 CenterZ=0 NormalX=0 NormalY=0 NormalZ=1 AngleXU=0 Radius=1.6
  constraints (3):
    c: Diameter(g0) = 3.2
    c: DistanceX(g-1,g0) = 44.5
    c: DistanceY(g0,g-1) = 22
FEATURE [PartDesign::Pocket] Pocket032
  BaseFeature = -> Pad008
  Direction = (1,1,1)
  Length = 11
  Length2 = 10
  Placement = pos=(0,0,0) rot=(1,0,0;1.5708rad)
  Profile = -> Sketch047
  Reversed = true
  Type = 4
FEATURE [Sketcher::SketchObject] Sketch048
  FullyConstrained = true
  MapMode = 5
  Placement = pos=(0,-15,-2e-15) rot=(1,0,0;1.5708rad)
  Support = -> [DatumPlane003]
  sketch-geometry (7):
    g0: LineSegment StartX=-42.9123 StartY=-24.75 StartZ=0 EndX=-41.3246 EndY=-22 EndZ=0
    g1: LineSegment StartX=-41.3246 StartY=-22 StartZ=0 EndX=-42.9123 EndY=-19.25 EndZ=0
    g2: LineSegment StartX=-42.9123 StartY=-19.25 StartZ=0 EndX=-46.0877 EndY=-19.25 EndZ=0
    g3: LineSegment StartX=-46.0877 StartY=-19.25 StartZ=0 EndX=-47.6754 EndY=-22 EndZ=0
    g4: LineSegment StartX=-47.6754 StartY=-22 StartZ=0 EndX=-46.0877 EndY=-24.75 EndZ=0
    g5: LineSegment StartX=-46.0877 StartY=-24.75 StartZ=0 EndX=-42.9123 EndY=-24.75 EndZ=0
    g6: Circle CenterX=-44.5 CenterY=-22 CenterZ=0 NormalX=0 NormalY=0 NormalZ=1 AngleXU=0 Radius=3.17543
  constraints (17):
    c: Coincident(g0,g1)
    c: Coincident(g1,g2)
    c: Coincident(g2,g3)
    c: Coincident(g3,g4)
    c: Coincident(g4,g5)
    c: Coincident(g5,g0)
    c: Equal(g0, g1-g5) x5
    c: PointOnObject(g0,g6)
    c: PointOnObject(g1,g6)
    c: PointOnObject(g2,g6)
    c: PointOnObject(g3,g6)
    c: PointOnObject(g4,g6)
    c: PointOnObject(g5,g6)
    c: Horizontal(g5)
    c: DistanceY(g4,g2) = 5.5
    c: DistanceX(g6,g-1) = 44.5
    c: DistanceY(g6,g-1) = 22
FEATURE [PartDesign::Pocket] Pocket033
  BaseFeature = -> Pocket032
  Direction = (1,1,1)
  Length = 2.5
  Length2 = 100
  Placement = pos=(0,0,0) rot=(1,0,0;1.5708rad)
  Profile = -> Sketch048
  Type = 0
FEATURE [Sketcher::SketchObject] Sketch049
  FullyConstrained = false
  MapMode = 5
  Placement = pos=(0,0,0) rot=(1,0,0;1.5708rad)
  Support = -> [XZ_Plane]
  sketch-geometry (3):
    g0: LineSegment StartX=16.9846 StartY=14.2418 StartZ=0 EndX=-0.028123 EndY=18.4303 EndZ=0
    g1: LineSegment StartX=-0.028123 StartY=18.4303 StartZ=0 EndX=-0.609563 EndY=14.2418 EndZ=0
    g2: LineSegment StartX=-0.609563 StartY=14.2418 StartZ=0 EndX=16.9846 EndY=14.2418 EndZ=0
  constraints (4):
    c: Coincident(g0,g1)
    c: Coincident(g1,g2)
    c: Horizontal(g2)
    c: Coincident(g0,g2)
FEATURE [PartDesign::Pocket] Pocket034
  BaseFeature = -> Pocket033
  Direction = (1,1,1)
  Length = 4.6
  Length2 = 100
  Placement = pos=(0,0,0) rot=(1,0,0;1.5708rad)
  Profile = -> Sketch049
  Reversed = true
  Type = 0
FEATURE [PartDesign::Plane] DatumPlane008
  Length = 84.7386
  MapMode = 45
  Placement = pos=(-36,-12.0242,18.5505) rot=(-0.105513,-0.095338,0.989837;1.47152rad)
  ResizeMode = 0
  Support = -> [Pocket034]
  Width = 175.608
FEATURE [Sketcher::SketchObject] Sketch050
  ExternalGeometry = -> [Pocket034]
  FullyConstrained = false
  MapMode = 5
  Placement = pos=(-36,-12.0242,18.5505) rot=(-0.105513,-0.095338,0.989837;1.47152rad)
  Support = -> [DatumPlane008]
  sketch-geometry (4):
    g0: LineSegment StartX=-1.97232 StartY=8.44829 StartZ=0 EndX=-3.73392 EndY=6.86178 EndZ=0
    g1: LineSegment StartX=-3.73392 StartY=6.86178 StartZ=0 EndX=-4.48148 EndY=13.7877 EndZ=0
    g2: LineSegment StartX=-1.97232 StartY=8.44829 StartZ=0 EndX=-0.900308 EndY=14.0764 EndZ=0
    g3: LineSegment StartX=-0.900308 StartY=14.0764 StartZ=0 EndX=-4.48148 EndY=13.7877 EndZ=0
  constraints (6):
    c: PointOnObject(g0,g-4)
    c: Coincident(g0,g1)
    c: Coincident(g0,g2)
    c: Coincident(g2,g3)
    c: Coincident(g3,g1)
    c: PointOnObject(g1,g-4)
FEATURE [PartDesign::Pad] Pad009
  BaseFeature = -> Pocket034
  Direction = (1,1,1)
  Length = 1.5
  Length2 = 100
  Placement = pos=(0,0,0) rot=(1,0,0;1.5708rad)
  Profile = -> Sketch050
  Type = 0
FEATURE [PartDesign::Chamfer] Chamfer002
  Angle = 45
  Base = -> Pad009 [Edge463]
  BaseFeature = -> Pad009
  ChamferType = 0
  FlipDirection = false
  Placement = pos=(0,0,0) rot=(1,0,0;1.5708rad)
  Size = 1
  Size2 = 1
  SupportTransform = false
  UseAllEdges = false
FEATURE [PartDesign::Plane] DatumPlane009
  Length = 158.62
  MapMode = 5
  Placement = pos=(0,-1.6,-4e-16) rot=(-1,0,0;1.5708rad)
  ResizeMode = 0
  Support = -> [Chamfer002]
  Width = 110.938
FEATURE [Sketcher::SketchObject] Sketch051
  ExternalGeometry = -> [Chamfer002]
  FullyConstrained = false
  MapMode = 5
  Placement = pos=(0,-1.6,-4e-16) rot=(-1,0,0;1.5708rad)
  Support = -> [DatumPlane009]
  sketch-geometry (7):
    g0: LineSegment StartX=37.649 StartY=-8.93254 StartZ=0 EndX=37.649 EndY=0 EndZ=0
    g1: LineSegment StartX=37.649 StartY=0 StartZ=0 EndX=35.4387 EndY=0 EndZ=0
    g2: LineSegment StartX=35.4387 StartY=0 StartZ=0 EndX=32.8416 EndY=0.62049 EndZ=0
    g3: LineSegment StartX=32.8416 StartY=0.62049 StartZ=0 EndX=31.2273 EndY=0.62049 EndZ=0
    g4: LineSegment StartX=31.2273 StartY=0.62049 StartZ=0 EndX=31.2146 EndY=-6.22857 EndZ=0
    g5: LineSegment StartX=31.2146 StartY=-6.22857 StartZ=0 EndX=31.2146 EndY=-9.64173 EndZ=0
    g6: LineSegment StartX=31.2146 StartY=-9.64173 StartZ=0 EndX=37.649 EndY=-8.93254 EndZ=0
  constraints (12):
    c: Vertical(g0)
    c: Coincident(g0,g1)
    c: Horizontal(g1)
    c: Coincident(g1,g2)
    c: Coincident(g2,g3)
    c: Horizontal(g3)
    c: Coincident(g3,g4)
    c: Coincident(g4,g5)
    c: Vertical(g5)
    c: Coincident(g5,g6)
    c: Coincident(g6,g0)
    c: PointOnObject(g-3,g1)
FEATURE [PartDesign::Pocket] Pocket035
  BaseFeature = -> Chamfer002
  Direction = (1,1,1)
  Length = 8.4
  Length2 = 100
  Placement = pos=(0,0,0) rot=(1,0,0;1.5708rad)
  Profile = -> Sketch051
  Type = 0
FEATURE [Sketcher::SketchObject] Sketch052
  ExternalGeometry = -> [Pocket035]
  FullyConstrained = true
  MapMode = 5
  Placement = pos=(0,-1.6,-4e-16) rot=(-1,0,0;1.5708rad)
  Support = -> [DatumPlane009]
  sketch-geometry (4):
    g0: LineSegment StartX=29 StartY=-17.75 StartZ=0 EndX=28 EndY=-17.75 EndZ=0
    g1: LineSegment StartX=28 StartY=-17.75 StartZ=0 EndX=28 EndY=-4.75 EndZ=0
    g2: LineSegment StartX=28 StartY=-4.75 StartZ=0 EndX=29 EndY=-3.75 EndZ=0
    g3: LineSegment StartX=29 StartY=-3.75 StartZ=0 EndX=29 EndY=-17.75 EndZ=0
  constraints (11):
    c: Coincident(g-3,g0)
    c: Horizontal(g0)
    c: Coincident(g0,g1)
    c: Vertical(g1)
    c: Coincident(g1,g2)
    c: Coincident(g2,g3)
    c: Coincident(g3,g0)
    c: Vertical(g3)
    c: Angle(g2,g3) = 0.785398
    c: DistanceY(g3,g3) = 14
    c: DistanceX(g0,g0) = 1
FEATURE [PartDesign::Pocket] Pocket036
  BaseFeature = -> Pocket035
  Direction = (1,1,1)
  Length = 15
  Length2 = 100
  Placement = pos=(0,0,0) rot=(1,0,0;1.5708rad)
  Profile = -> Sketch052
  Type = 0
FEATURE [Sketcher::SketchObject] Sketch053
  ExternalGeometry = -> [Pocket036]
  FullyConstrained = false
  MapMode = 5
  Placement = pos=(0,-1.6,-4e-16) rot=(-1,0,0;1.5708rad)
  Support = -> [DatumPlane009]
  sketch-geometry (7):
    g0: LineSegment StartX=29 StartY=2.25 StartZ=0 EndX=21.25 EndY=-5.5 EndZ=0
    g1: LineSegment StartX=29 StartY=-3.75 StartZ=0 EndX=29 EndY=2.25 EndZ=0
    g2: LineSegment StartX=29 StartY=-3.75 StartZ=0 EndX=17.3693 EndY=-15.3807 EndZ=0
    g3: LineSegment StartX=17.3693 StartY=-15.3807 StartZ=0 EndX=3.11931 EndY=-15.3807 EndZ=0
    g4: LineSegment StartX=0 StartY=-18.5 StartZ=0 EndX=3.11931 EndY=-15.3807 EndZ=0
    g5: LineSegment StartX=21.25 StartY=-5.5 StartZ=0 EndX=0 EndY=-5.5 EndZ=0
    g6: LineSegment StartX=0 StartY=-5.5 StartZ=0 EndX=0 EndY=-18.5 EndZ=0
  constraints (16):
    c: Coincident(g-3,g0)
    c: Coincident(g1,g0)
    c: Angle(g0,g1) = 0.785398
    c: Coincident(g1,g2)
    c: Coincident(g2,g3)
    c: Horizontal(g3)
    c: Angle(g1,g2) = 2.35619
    c: Coincident(g-3,g1)
    c: Coincident(g-4,g4)
    c: Coincident(g4,g3)
    c: Coincident(g0,g5)
    c: Horizontal(g5)
    c: Coincident(g6,g4)
    c: Angle(g4,g6) = 0.785398
    c: Coincident(g5,g6)
    c: Coincident(g5,g-5)
FEATURE [Sketcher::SketchObject] Sketch054
  ExternalGeometry = -> [Pocket036]
  FullyConstrained = false
  MapMode = 5
  Placement = pos=(0,-1.6,-4e-16) rot=(-1,0,0;1.5708rad)
  Support = -> [DatumPlane009]
  sketch-geometry (5):
    g0: LineSegment StartX=28 StartY=-6.59491 StartZ=0 EndX=0 EndY=-5.5 EndZ=0
    g1: LineSegment StartX=0 StartY=-5.5 StartZ=0 EndX=0 EndY=-19.2221 EndZ=0
    g2: LineSegment StartX=0 StartY=-19.2221 StartZ=0 EndX=13.787 EndY=-16.6278 EndZ=0
    g3: LineSegment StartX=13.787 StartY=-16.6278 StartZ=0 EndX=28 EndY=-16.6278 EndZ=0
    g4: LineSegment StartX=28 StartY=-16.6278 StartZ=0 EndX=28 EndY=-6.59491 EndZ=0
  constraints (10):
    c: Coincident(g-3,g0)
    c: Coincident(g0,g-4)
    c: Coincident(g0,g1)
    c: PointOnObject(g1,g-2)
    c: Coincident(g1,g2)
    c: Coincident(g2,g3)
    c: Horizontal(g3)
    c: Coincident(g3,g4)
    c: Coincident(g4,g0)
    c: Vertical(g4)
FEATURE [PartDesign::Pad] Pad010
  BaseFeature = -> Pocket036
  Direction = (1,1,1)
  Length = 3
  Length2 = 100
  Placement = pos=(0,0,0) rot=(1,0,0;1.5708rad)
  Profile = -> Sketch054
  Reversed = true
  Type = 0
FEATURE [PartDesign::Pocket] Pocket037
  BaseFeature = -> Pad010
  Direction = (1,1,1)
  Length = 3.9
  Length2 = 100
  Placement = pos=(0,0,0) rot=(1,0,0;1.5708rad)
  Profile = -> Sketch053
  Type = 0
FEATURE [PartDesign::Chamfer] Chamfer003
  Angle = 45
  Base = -> Pocket037 [Edge206]
  BaseFeature = -> Pocket037
  ChamferType = 0
  FlipDirection = false
  Placement = pos=(0,0,0) rot=(1,0,0;1.5708rad)
  Size = 1
  Size2 = 1
  SupportTransform = false
  UseAllEdges = false
FEATURE [Sketcher::SketchObject] Sketch055
  FullyConstrained = false
  MapMode = 5
  Placement = pos=(0,0,0) rot=(1,0,0;1.5708rad)
  Support = -> [XZ_Plane]
  sketch-geometry (4):
    g0: LineSegment StartX=0 StartY=32.353 StartZ=0 EndX=-51.5297 EndY=32.353 EndZ=0
    g1: LineSegment StartX=-51.5297 StartY=32.353 StartZ=0 EndX=-51.5297 EndY=39.5928 EndZ=0
    g2: LineSegment StartX=-51.5297 StartY=39.5928 StartZ=0 EndX=0 EndY=39.5928 EndZ=0
    g3: LineSegment StartX=0 StartY=39.5928 StartZ=0 EndX=0 EndY=32.353 EndZ=0
  constraints (9):
    c: Coincident(g0,g1)
    c: Coincident(g1,g2)
    c: Coincident(g2,g3)
    c: Coincident(g3,g0)
    c: Horizontal(g0)
    c: Horizontal(g2)
    c: Vertical(g1)
    c: Vertical(g3)
    c: PointOnObject(g0,g-2)
FEATURE [PartDesign::Pocket] Pocket038
  BaseFeature = -> Chamfer003
  Direction = (1,1,1)
  Length = 1.6
  Length2 = 100
  Placement = pos=(0,0,0) rot=(1,0,0;1.5708rad)
  Profile = -> Sketch055
  Reversed = true
  Type = 0
FEATURE [PartDesign::Pocket] Pocket039
  BaseFeature = -> Pocket038
  Direction = (1,1,1)
  Length = 0.5
  Length2 = 100
  Placement = pos=(0,0,0) rot=(1,0,0;1.5708rad)
  Profile = -> Pocket038 [Face8]
  Type = 0
FEATURE [Sketcher::SketchObject] Sketch056
  FullyConstrained = false
  MapMode = 5
  Placement = pos=(0,0,0) rot=(1,0,0;1.5708rad)
  Support = -> [XZ_Plane]
  sketch-geometry (3):
    g0: LineSegment StartX=-49.9014 StartY=28.2671 StartZ=0 EndX=-36.6825 EndY=41.4859 EndZ=0
    g1: LineSegment StartX=-36.6825 StartY=41.4859 StartZ=0 EndX=-49.9014 EndY=41.4859 EndZ=0
    g2: LineSegment StartX=-49.9014 StartY=41.4859 StartZ=0 EndX=-49.9014 EndY=28.2671 EndZ=0
  constraints (6):
    c: Coincident(g0,g1)
    c: Horizontal(g1)
    c: Coincident(g1,g2)
    c: Coincident(g2,g0)
    c: Vertical(g2)
    c: Angle(g1,g0) = 0.785398
FEATURE [PartDesign::Pocket] Pocket040
  BaseFeature = -> Pocket039
  Direction = (1,1,1)
  Length = 3.5
  Length2 = 100
  Placement = pos=(0,0,0) rot=(1,0,0;1.5708rad)
  Profile = -> Sketch056
  Reversed = true
  Type = 0
FEATURE [PartDesign::Chamfer] Chamfer004
  Angle = 45
  Base = -> Pocket040 [Edge749]
  BaseFeature = -> Pocket040
  ChamferType = 0
  FlipDirection = false
  Placement = pos=(0,0,0) rot=(1,0,0;1.5708rad)
  Size = 1
  Size2 = 1
  SupportTransform = false
  UseAllEdges = false
FEATURE [Sketcher::SketchObject] Sketch057
  ExternalGeometry = -> [Chamfer004]
  FullyConstrained = true
  MapMode = 5
  Placement = pos=(0,0,0) rot=(1,0,0;1.5708rad)
  Support = -> [XZ_Plane]
  sketch-geometry (8):
    g0: LineSegment StartX=80.1957 StartY=26.9457 StartZ=0 EndX=79.6654 EndY=26.4154 EndZ=0
    g1: LineSegment StartX=0.25 StartY=33.25 StartZ=0 EndX=0.25 EndY=32.49 EndZ=0
    g2: LineSegment StartX=0.25 StartY=32.49 StartZ=0 EndX=65 EndY=32.49 EndZ=0
    g3: LineSegment StartX=65 StartY=33.24 StartZ=0 EndX=0.25 EndY=33.25 EndZ=0
    g4: LineSegment StartX=0.25 StartY=33.25 StartZ=0 EndX=0.25 EndY=32.49 EndZ=0
    g5: ArcOfCircle CenterX=65 CenterY=11.75 CenterZ=0 NormalX=0 NormalY=0 NormalZ=1 AngleXU=0 Radius=20.74 StartAngle=0.785398 EndAngle=1.5708
    g6: ArcOfCircle CenterX=65 CenterY=11.75 CenterZ=0 NormalX=0 NormalY=0 NormalZ=1 AngleXU=0 Radius=21.49 StartAngle=0.785398 EndAngle=1.5708
    g7: LineSegment StartX=65 StartY=11.75 StartZ=0 EndX=65 EndY=32.49 EndZ=0
  constraints (22):
    c: Coincident(g1,g2)
    c: Horizontal(g2)
    c: Coincident(g3,g1)
    c: Coincident(g3,g4)
    c: Coincident(g4,g1)
    c: Coincident(g5,g-5)
    c: Coincident(g5,g0)
    c: Coincident(g2,g5)
    c: PointOnObject(g5,g0)
    c: Coincident(g6,g5)
    c: Coincident(g0,g6)
    c: Coincident(g7,g-5)
    c: Vertical(g7)
    c: Coincident(g7,g2)
    c: Angle(g0,g7) = 0.785398
    c: Distance(g0) = 0.75
    c: Vertical(g1)
    c: DistanceX(g-6,g1) = 0.25
    c: DistanceY(g-6,g1) = 0.25
    c: Coincident(g3,g6)
    c: PointOnObject(g3,g7)
    c: DistanceY(g-7,g3) = 0.25
FEATURE [PartDesign::Fillet] Fillet001
  Base = -> Chamfer004 [Edge628]
  BaseFeature = -> Chamfer004
  Placement = pos=(0,0,0) rot=(1,0,0;1.5708rad)
  Radius = 10
  SupportTransform = false
  UseAllEdges = false
FEATURE [Sketcher::SketchObject] Sketch058
  ExternalGeometry = -> [Fillet001]
  FullyConstrained = false
  MapMode = 5
  Placement = pos=(0,0,0) rot=(1,0,0;1.5708rad)
  Support = -> [XZ_Plane]
  sketch-geometry (9):
    g0: ArcOfCircle CenterX=63.75 CenterY=2.5 CenterZ=0 NormalX=0 NormalY=0 NormalZ=1 AngleXU=0 Radius=22.5 StartAngle=4.71239 EndAngle=6.28319
    g1: ArcOfCircle CenterX=10.1397 CenterY=3.75 CenterZ=0 NormalX=0 NormalY=0 NormalZ=1 AngleXU=0 Radius=6 StartAngle=4.71239 EndAngle=5.49779
    g2: LineSegment StartX=10.1397 StartY=-2.25 StartZ=0 EndX=10.1796 EndY=-4.79798 EndZ=0
    g3: LineSegment StartX=10.1796 StartY=-4.79798 StartZ=0 EndX=15.6044 EndY=-4.38092 EndZ=0
    g4: LineSegment StartX=15.6044 StartY=-4.38092 StartZ=0 EndX=14.3824 EndY=-0.492649 EndZ=0
    g5: LineSegment StartX=63.75 StartY=-20 StartZ=0 EndX=63.8164 EndY=-30.4013 EndZ=0
    g6: LineSegment StartX=63.8164 StartY=-30.4013 StartZ=0 EndX=97.6629 EndY=-30.4013 EndZ=0
    g7: LineSegment StartX=97.6629 StartY=-30.4013 StartZ=0 EndX=97.6629 EndY=-7.23354 EndZ=0
    g8: LineSegment StartX=97.6629 StartY=-7.23354 StartZ=0 EndX=86.25 EndY=2.50006 EndZ=0
  constraints (21):
    c: PointOnObject(g1,g-4)
    c: PointOnObject(g1,g-3)
    c: Tangent(g1,g-3)
    c: Tangent(g1,g-4)
    c: Diameter(g1) = 12
    c: Coincident(g1,g2)
    c: Coincident(g2,g3)
    c: Coincident(g3,g4)
    c: Coincident(g4,g1)
    c: PointOnObject(g0,g-5)
    c: PointOnObject(g0,g-6)
    c: Tangent(g0,g-6)
    c: Tangent(g0,g-5)
    c: Diameter(g0) = 45
    c: Coincident(g0,g5)
    c: Coincident(g5,g6)
    c: Horizontal(g6)
    c: Coincident(g6,g7)
    c: Vertical(g7)
    c: Coincident(g7,g8)
    c: Coincident(g8,g0)
FEATURE [PartDesign::Pocket] Pocket041
  BaseFeature = -> Fillet001
  Direction = (1,1,1)
  Length = 5
  Length2 = 100
  Placement = pos=(0,0,0) rot=(1,0,0;1.5708rad)
  Profile = -> Sketch058
  Reversed = true
  Type = 1
FEATURE [Sketcher::SketchObject] Sketch059
  FullyConstrained = false
  MapMode = 5
  Placement = pos=(0,-5.5,6.1e-15) rot=(-1,0,0;1.5708rad)
  Support = -> [Pocket041]
  sketch-geometry (4):
    g0: LineSegment StartX=17.19 StartY=-14.8762 StartZ=0 EndX=1.46231 EndY=-14.8762 EndZ=0
    g1: LineSegment StartX=1.46231 StartY=-14.8762 StartZ=0 EndX=1.46231 EndY=-5.86709 EndZ=0
    g2: LineSegment StartX=1.46231 StartY=-5.86709 StartZ=0 EndX=17.19 EndY=-5.86709 EndZ=0
    g3: LineSegment StartX=17.19 StartY=-5.86709 StartZ=0 EndX=17.19 EndY=-14.8762 EndZ=0
  constraints (8):
    c: Coincident(g0,g1)
    c: Coincident(g1,g2)
    c: Coincident(g2,g3)
    c: Coincident(g3,g0)
    c: Horizontal(g0)
    c: Horizontal(g2)
    c: Vertical(g1)
    c: Vertical(g3)
FEATURE [PartDesign::Pocket] Pocket042
  BaseFeature = -> Pocket041
  Direction = (1,1,1)
  Length = 5
  Length2 = 100
  Placement = pos=(0,0,0) rot=(1,0,0;1.5708rad)
  Profile = -> Sketch059
  Type = 0
FEATURE [PartDesign::Chamfer] Chamfer005
  Angle = 45
  Base = -> Pocket042 [Edge657]
  BaseFeature = -> Pocket042
  ChamferType = 0
  FlipDirection = false
  Placement = pos=(0,0,0) rot=(1,0,0;1.5708rad)
  Size = 4
  Size2 = 1
  SupportTransform = false
  UseAllEdges = false
FEATURE [Sketcher::SketchObject] Sketch060
  FullyConstrained = true
  MapMode = 5
  Placement = pos=(0,-15,-2e-15) rot=(1,0,0;1.5708rad)
  Support = -> [DatumPlane003]
  sketch-geometry (4):
    g0: LineSegment StartX=-22 StartY=34.9 StartZ=0 EndX=-22 EndY=48.9 EndZ=0
    g1: LineSegment StartX=-22 StartY=48.9 StartZ=0 EndX=-36 EndY=48.9 EndZ=0
    g2: LineSegment StartX=-36 StartY=48.9 StartZ=0 EndX=-50 EndY=34.9 EndZ=0
    g3: LineSegment StartX=-50 StartY=34.9 StartZ=0 EndX=-22 EndY=34.9 EndZ=0
  constraints (12):
    c: Vertical(g0)
    c: Coincident(g1,g2)
    c: Coincident(g2,g3)
    c: Coincident(g3,g0)
    c: Horizontal(g3)
    c: DistanceY(g-1,g0) = 34.9
    c: Horizontal(g1)
    c: Angle(g3,g2) = 0.785398
    c: DistanceX(g2,g-1) = 50
    c: DistanceX(g2,g1) = 14
    c: DistanceX(g3,g3) = 28
    c: Coincident(g1,g0)
FEATURE [PartDesign::Pad] Pad011
  BaseFeature = -> Chamfer005
  Direction = (1,1,1)
  Length = 13.4
  Length2 = 100
  Placement = pos=(0,0,0) rot=(1,0,0;1.5708rad)
  Profile = -> Sketch060
  Reversed = true
  Type = 0
FEATURE [PartDesign::Chamfer] Chamfer006
  Angle = 45
  Base = -> Pad011 [Edge872,Edge873,Edge874]
  BaseFeature = -> Pad011
  ChamferType = 0
  FlipDirection = false
  Placement = pos=(0,0,0) rot=(1,0,0;1.5708rad)
  Size = 2
  Size2 = 1
  SupportTransform = false
  UseAllEdges = false
FEATURE [Sketcher::SketchObject] Sketch061
  FullyConstrained = false
  MapMode = 5
  Placement = pos=(0,0,0) rot=(1,0,0;1.5708rad)
  Support = -> [XZ_Plane]
  sketch-geometry (19):
    g0: LineSegment StartX=-50.9533 StartY=35 StartZ=0 EndX=-37.7023 EndY=48.2509 EndZ=0
    g1: LineSegment StartX=-37.7023 StartY=48.2509 StartZ=0 EndX=-35.3514 EndY=45.9 EndZ=0
    g2: LineSegment StartX=-35.3514 StartY=45.9 StartZ=0 EndX=-32.2947 EndY=45.9 EndZ=0
    g3: LineSegment StartX=-32.2947 StartY=45.9 StartZ=0 EndX=-32.2947 EndY=46.9 EndZ=0
    g4: LineSegment StartX=-32.2947 StartY=46.9 StartZ=0 EndX=-33.2947 EndY=46.9 EndZ=0
    g5: LineSegment StartX=-33.2947 StartY=46.9 StartZ=0 EndX=-33.2947 EndY=47.9 EndZ=0
    g6: LineSegment StartX=-33.2947 StartY=47.9 StartZ=0 EndX=-32.2947 EndY=47.9 EndZ=0
    g7: LineSegment StartX=-32.2947 StartY=47.9 StartZ=0 EndX=-32.2947 EndY=48.9 EndZ=0
    g8: LineSegment StartX=-32.2947 StartY=48.9 StartZ=0 EndX=-26.2947 EndY=48.9 EndZ=0
    g9: LineSegment StartX=-26.2947 StartY=48.9 StartZ=0 EndX=-26.2947 EndY=47.9 EndZ=0
    g10: LineSegment StartX=-26.2947 StartY=47.9 StartZ=0 EndX=-25.2947 EndY=47.9 EndZ=0
    g11: LineSegment StartX=-25.2947 StartY=47.9 StartZ=0 EndX=-25.2947 EndY=46.9 EndZ=0
    g12: LineSegment StartX=-25.2947 StartY=46.9 StartZ=0 EndX=-26.2947 EndY=46.9 EndZ=0
    g13: LineSegment StartX=-26.2947 StartY=46.9 StartZ=0 EndX=-26.2947 EndY=45.9 EndZ=0
    g14: LineSegment StartX=-26.2947 StartY=45.9 StartZ=0 EndX=-24 EndY=45.9 EndZ=0
    g15: LineSegment StartX=-24 StartY=45.9 StartZ=0 EndX=-24 EndY=41 EndZ=0
    g16: LineSegment StartX=-24 StartY=41 StartZ=0 EndX=-22 EndY=41 EndZ=0
    g17: LineSegment StartX=-22 StartY=41 StartZ=0 EndX=-22 EndY=35 EndZ=0
    g18: LineSegment StartX=-22 StartY=35 StartZ=0 EndX=-50.9533 EndY=35 EndZ=0
  constraints (54):
    c: Coincident(g0,g1)
    c: Coincident(g1,g2)
    c: Horizontal(g2)
    c: Coincident(g2,g3)
    c: Vertical(g3)
    c: Coincident(g3,g4)
    c: Horizontal(g4)
    c: Coincident(g4,g5)
    c: Vertical(g5)
    c: Coincident(g5,g6)
    c: Horizontal(g6)
    c: Coincident(g6,g7)
    c: Vertical(g7)
    c: Coincident(g7,g8)
    c: Horizontal(g8)
    c: Coincident(g8,g9)
    c: Vertical(g9)
    c: Coincident(g9,g10)
    c: Horizontal(g10)
    c: Coincident(g10,g11)
    c: Vertical(g11)
    c: Coincident(g11,g12)
    c: Horizontal(g12)
    c: Coincident(g12,g13)
    c: Vertical(g13)
    c: Coincident(g13,g14)
    c: Horizontal(g14)
    c: Coincident(g14,g15)
    c: Vertical(g15)
    c: Coincident(g15,g16)
    c: Horizontal(g16)
    c: Coincident(g16,g17)
    c: Vertical(g17)
    c: Coincident(g17,g18)
    c: Coincident(g18,g0)
    c: Horizontal(g18)
    c: DistanceX(g8,g8) = 6
    c: DistanceY(g5,g5) = 1
    c: DistanceY(g11,g11) = 1
    c: DistanceY(g7,g7) = 1
    c: DistanceY(g9,g9) = 1
    c: PointOnObject(g3,g7)
    c: PointOnObject(g12,g9)
    c: DistanceX(g10,g10) = 1
    c: DistanceX(g6,g6) = 1
    c: DistanceY(g13,g13) = 1
    c: DistanceY(g3,g3) = 1
    c: DistanceY(g17,g17) = 6
    c: DistanceY(g-1,g17) = 35
    c: DistanceX(g16,g16) = 2
    c: DistanceX(g17,g-1) = 22
    c: DistanceY(g17,g8) = 13.9
    c: Angle(g18,g0) = 0.785398
    c: Perpendicular(g0,g1)
FEATURE [PartDesign::Pocket] Pocket043
  BaseFeature = -> Chamfer006
  Direction = (1,1,1)
  Length = 8
  Length2 = 100
  Placement = pos=(0,0,0) rot=(1,0,0;1.5708rad)
  Profile = -> Sketch061
  Reversed = true
  Type = 0
FEATURE [Sketcher::SketchObject] Sketch062
  FullyConstrained = false
  MapMode = 5
  Placement = pos=(0,-15,-2e-15) rot=(1,0,0;1.5708rad)
  Support = -> [DatumPlane003]
  sketch-geometry (4):
    g0: LineSegment StartX=-43.4114 StartY=34.9088 StartZ=0 EndX=-49.9958 EndY=34.9088 EndZ=0
    g1: LineSegment StartX=-49.9958 StartY=34.9088 StartZ=0 EndX=-49.9958 EndY=32.971 EndZ=0
    g2: LineSegment StartX=-49.9958 StartY=32.971 StartZ=0 EndX=-43.4114 EndY=32.971 EndZ=0
    g3: LineSegment StartX=-43.4114 StartY=32.971 StartZ=0 EndX=-43.4114 EndY=34.9088 EndZ=0
  constraints (8):
    c: Horizontal(g0)
    c: Coincident(g0,g1)
    c: Vertical(g1)
    c: Coincident(g1,g2)
    c: Horizontal(g2)
    c: Coincident(g2,g3)
    c: Coincident(g3,g0)
    c: Vertical(g3)
FEATURE [PartDesign::Pad] Pad012
  BaseFeature = -> Pocket043
  Direction = (1,1,1)
  Length = 13.4
  Length2 = 100
  Placement = pos=(0,0,0) rot=(1,0,0;1.5708rad)
  Profile = -> Sketch062
  Reversed = true
  Type = 0
FEATURE [PartDesign::Fillet] Fillet002
  Base = -> Pad012 [Edge180]
  BaseFeature = -> Pad012
  Placement = pos=(0,0,0) rot=(1,0,0;1.5708rad)
  Radius = 1
  SupportTransform = false
  UseAllEdges = false
FEATURE [Sketcher::SketchObject] Sketch063
  FullyConstrained = false
  MapMode = 5
  Placement = pos=(-42.45,4.8e-15,42.45) rot=(-0.382683,0,0.92388;3.14159rad)
  Support = -> [Fillet002]
  sketch-geometry (8):
    g0: LineSegment StartX=-6.97585 StartY=1.6 StartZ=0 EndX=1.02415 EndY=1.6 EndZ=0
    g1: LineSegment StartX=1.02415 StartY=1.6 StartZ=0 EndX=1.02415 EndY=9.6 EndZ=0
    g2: LineSegment StartX=1.02415 StartY=9.6 StartZ=0 EndX=-6.97585 EndY=9.6 EndZ=0
    g3: LineSegment StartX=-6.97585 StartY=9.6 StartZ=0 EndX=-6.97585 EndY=1.6 EndZ=0
    g4: LineSegment StartX=1.89073 StartY=1.6 StartZ=0 EndX=9.89073 EndY=1.6 EndZ=0
    g5: LineSegment StartX=9.89073 StartY=1.6 StartZ=0 EndX=9.89073 EndY=9.6 EndZ=0
    g6: LineSegment StartX=9.89073 StartY=9.6 StartZ=0 EndX=1.89073 EndY=9.6 EndZ=0
    g7: LineSegment StartX=1.89073 StartY=9.6 StartZ=0 EndX=1.89073 EndY=1.6 EndZ=0
  constraints (22):
    c: Coincident(g0,g1)
    c: Coincident(g1,g2)
    c: Coincident(g2,g3)
    c: Coincident(g3,g0)
    c: Horizontal(g0)
    c: Horizontal(g2)
    c: Vertical(g1)
    c: Vertical(g3)
    c: Coincident(g4,g5)
    c: Coincident(g5,g6)
    c: Coincident(g6,g7)
    c: Coincident(g7,g4)
    c: Horizontal(g4)
    c: Horizontal(g6)
    c: Vertical(g5)
    c: Vertical(g7)
    c: DistanceY(g-1,g0) = 1.6
    c: PointOnObject(g4,g0)
    c: DistanceX(g4,g4) = 8
    c: DistanceX(g0,g0) = 8
    c: DistanceY(g3,g3) = 8
    c: DistanceY(g7,g7) = 8
FEATURE [PartDesign::Pad] Pad013
  BaseFeature = -> Fillet002
  Direction = (1,1,1)
  Length = 1
  Length2 = 100
  Placement = pos=(0,0,0) rot=(1,0,0;1.5708rad)
  Profile = -> Sketch063
  Type = 0
FEATURE [Sketcher::SketchObject] Sketch064
  FullyConstrained = false
  MapMode = 5
  Placement = pos=(-43.1571,1.83e-14,43.1571) rot=(-0.382683,0,0.92388;3.14159rad)
  Support = -> [Pad013]
  sketch-geometry (8):
    g0: LineSegment StartX=-6.72226 StartY=1.83522 StartZ=0 EndX=0.777739 EndY=1.83522 EndZ=0
    g1: LineSegment StartX=0.777739 StartY=1.83522 StartZ=0 EndX=0.777739 EndY=7.33522 EndZ=0
    g2: LineSegment StartX=0.777739 StartY=7.33522 StartZ=0 EndX=-6.72226 EndY=7.33522 EndZ=0
    g3: LineSegment StartX=-6.72226 StartY=7.33522 StartZ=0 EndX=-6.72226 EndY=1.83522 EndZ=0
    g4: LineSegment StartX=2.1471 StartY=1.79286 StartZ=0 EndX=9.6471 EndY=1.79286 EndZ=0
    g5: LineSegment StartX=9.6471 StartY=1.79286 StartZ=0 EndX=9.6471 EndY=7.29286 EndZ=0
    g6: LineSegment StartX=9.6471 StartY=7.29286 StartZ=0 EndX=2.1471 EndY=7.29286 EndZ=0
    g7: LineSegment StartX=2.1471 StartY=7.29286 StartZ=0 EndX=2.1471 EndY=1.79286 EndZ=0
  constraints (20):
    c: Coincident(g0,g1)
    c: Coincident(g1,g2)
    c: Coincident(g2,g3)
    c: Coincident(g3,g0)
    c: Horizontal(g0)
    c: Horizontal(g2)
    c: Vertical(g1)
    c: Vertical(g3)
    c: Coincident(g4,g5)
    c: Coincident(g5,g6)
    c: Coincident(g6,g7)
    c: Coincident(g7,g4)
    c: Horizontal(g4)
    c: Horizontal(g6)
    c: Vertical(g5)
    c: Vertical(g7)
    c: DistanceX(g2,g2) = 7.5
    c: DistanceX(g6,g6) = 7.5
    c: DistanceY(g3,g3) = 5.5
    c: DistanceY(g7,g7) = 5.5
FEATURE [PartDesign::Pad] Pad014
  BaseFeature = -> Pad013
  Direction = (1,1,1)
  Length = 1
  Length2 = 100
  Placement = pos=(0,0,0) rot=(1,0,0;1.5708rad)
  Profile = -> Sketch064
  Type = 0
FEATURE [PartDesign::Chamfer] Chamfer007
  Angle = 45
  Base = -> Pad014 [Edge139,Edge148]
  BaseFeature = -> Pad014
  ChamferType = 0
  FlipDirection = false
  Placement = pos=(0,0,0) rot=(1,0,0;1.5708rad)
  Size = 0.99
  Size2 = 1
  SupportTransform = false
  UseAllEdges = false
FEATURE [PartDesign::Chamfer] Chamfer008
  Angle = 45
  Base = -> Chamfer007 [Face86,Face53]
  BaseFeature = -> Chamfer007
  ChamferType = 0
  FlipDirection = false
  Placement = pos=(0,0,0) rot=(1,0,0;1.5708rad)
  Size = 0.5
  Size2 = 1
  SupportTransform = false
  UseAllEdges = false
FEATURE [Sketcher::SketchObject] Sketch065
  FullyConstrained = false
  MapMode = 5
  Placement = pos=(0,0,0) rot=(1,0,0;1.5708rad)
  Support = -> [XZ_Plane]
  sketch-geometry (8):
    g0: LineSegment StartX=-49.0841 StartY=37.1415 StartZ=0 EndX=-47.3306 EndY=35.388 EndZ=0
    g1: LineSegment StartX=-47.3306 StartY=35.388 StartZ=0 EndX=-43.6298 EndY=39.0887 EndZ=0
    g2: LineSegment StartX=-43.6298 StartY=39.0887 StartZ=0 EndX=-45.3834 EndY=40.8423 EndZ=0
    g3: LineSegment StartX=-45.3834 StartY=40.8423 StartZ=0 EndX=-49.0841 EndY=37.1415 EndZ=0
    g4: LineSegment StartX=-42.78 StartY=43.4456 StartZ=0 EndX=-39.258 EndY=46.9677 EndZ=0
    g5: LineSegment StartX=-39.258 StartY=46.9677 StartZ=0 EndX=-37.5661 EndY=45.2758 EndZ=0
    g6: LineSegment StartX=-37.5661 StartY=45.2758 StartZ=0 EndX=-41.0882 EndY=41.7537 EndZ=0
    g7: LineSegment StartX=-41.0882 StartY=41.7537 StartZ=0 EndX=-42.78 EndY=43.4456 EndZ=0
  constraints (17):
    c: Coincident(g0,g1)
    c: Coincident(g1,g2)
    c: Coincident(g2,g3)
    c: Coincident(g3,g0)
    c: Coincident(g4,g5)
    c: Coincident(g5,g6)
    c: Coincident(g6,g7)
    c: Coincident(g7,g4)
    c: Perpendicular(g3,g0)
    c: Perpendicular(g2,g3)
    c: Perpendicular(g1,g2)
    c: Perpendicular(g7,g4)
    c: Perpendicular(g7,g6)
    c: Perpendicular(g5,g4)
    c: PointOnObject(g2,g4)
    c: Angle(g4,g-2) = 0.785398
    c: PointOnObject(g0,g4)
FEATURE [PartDesign::Pocket] Pocket044
  BaseFeature = -> Chamfer008
  Direction = (1,1,1)
  Length = 5
  Length2 = 100
  Placement = pos=(0,0,0) rot=(1,0,0;1.5708rad)
  Profile = -> Sketch065
  Reversed = true
  Type = 0
FEATURE [Sketcher::SketchObject] Sketch066
  FullyConstrained = true
  MapMode = 5
  Placement = pos=(0,-1.15e-14,34.99) rot=(0,0,1;3.14159rad)
  Support = -> [DatumPlane006]
  sketch-geometry (4):
    g0: LineSegment StartX=-51.5 StartY=9 StartZ=0 EndX=-51.9019 EndY=10.5 EndZ=0
    g1: LineSegment StartX=-51.9019 StartY=10.5 StartZ=0 EndX=-53.954 EndY=10.5 EndZ=0
    g2: LineSegment StartX=-53.954 StartY=10.5 StartZ=0 EndX=-54.5 EndY=9 EndZ=0
    g3: LineSegment StartX=-54.5 StartY=9 StartZ=0 EndX=-51.5 EndY=9 EndZ=0
  constraints (12):
    c: Coincident(g0,g1)
    c: Horizontal(g1)
    c: Coincident(g1,g2)
    c: Coincident(g2,g3)
    c: Coincident(g3,g0)
    c: Horizontal(g3)
    c: DistanceY(g-1,g0) = 9
    c: DistanceY(g2,g1) = 1.5
    c: Angle(g-2,g0) = 0.261799
    c: DistanceX(g0,g-1) = 51.5
    c: DistanceX(g3,g3) = 3
    c: Angle(g3,g2) = 1.22173
FEATURE [PartDesign::Pocket] Pocket045
  BaseFeature = -> Pocket044
  Direction = (1,1,1)
  Length = 2
  Length2 = 100
  Placement = pos=(0,0,0) rot=(1,0,0;1.5708rad)
  Profile = -> Sketch066
  Type = 0
FEATURE [PartDesign::Chamfer] Chamfer009
  Angle = 45
  Base = -> Pocket045 [Edge356]
  BaseFeature = -> Pocket045
  ChamferType = 0
  FlipDirection = false
  Placement = pos=(0,0,0) rot=(1,0,0;1.5708rad)
  Size = 0.95
  Size2 = 1
  SupportTransform = false
  UseAllEdges = false
FEATURE [Sketcher::SketchObject] Sketch067
  FullyConstrained = true
  MapMode = 5
  Placement = pos=(65,0,2.55e-14) rot=(0.707107,0,-0.707107;3.14159rad)
  Support = -> [DatumPlane002]
  sketch-geometry (4):
    g0: LineSegment StartX=-31.75 StartY=10.1 StartZ=0 EndX=-31.25 EndY=10.1 EndZ=0
    g1: LineSegment StartX=-31.25 StartY=10.1 StartZ=0 EndX=-31.25 EndY=9.1 EndZ=0
    g2: LineSegment StartX=-31.25 StartY=9.1 StartZ=0 EndX=-31.75 EndY=9.1 EndZ=0
    g3: LineSegment StartX=-31.75 StartY=9.1 StartZ=0 EndX=-31.75 EndY=10.1 EndZ=0
  constraints (12):
    c: Coincident(g0,g1)
    c: Coincident(g1,g2)
    c: Coincident(g2,g3)
    c: Coincident(g3,g0)
    c: Horizontal(g0)
    c: Horizontal(g2)
    c: Vertical(g1)
    c: Vertical(g3)
    c: Distance(g-1,g2) = 9.1
    c: Distance(g3) = 1
    c: DistanceX(g2,g2) = 0.5
    c: DistanceX(g1,g-1) = 31.25
FEATURE [PartDesign::Pocket] Pocket046
  BaseFeature = -> Chamfer009
  Direction = (1,1,1)
  Length = 150
  Length2 = 100
  Placement = pos=(0,0,0) rot=(1,0,0;1.5708rad)
  Profile = -> Sketch067
  Reversed = true
  Type = 0
FEATURE [PartDesign::Groove] Groove003
  Angle = 45
  Axis = (0,-1,2e-16)
  Base = (65,5,11.75)
  BaseFeature = -> Pocket046
  Placement = pos=(0,0,0) rot=(1,0,0;1.5708rad)
  Profile = -> Sketch067
  ReferenceAxis = -> Sketch015 [Edge1]
  Reversed = true
FEATURE [Sketcher::SketchObject] Sketch068
  FullyConstrained = true
  MapMode = 5
  Placement = pos=(26.625,-3.4e-15,-26.625) rot=(-0.382683,0,0.92388;3.14159rad)
  Support = -> [DatumPlane004]
  sketch-geometry (4):
    g0: LineSegment StartX=-74.37 StartY=9.1 StartZ=0 EndX=-73.77 EndY=9.1 EndZ=0
    g1: LineSegment StartX=-73.77 StartY=9.1 StartZ=0 EndX=-73.77 EndY=10.1 EndZ=0
    g2: LineSegment StartX=-73.77 StartY=10.1 StartZ=0 EndX=-74.37 EndY=10.1 EndZ=0
    g3: LineSegment StartX=-74.37 StartY=10.1 StartZ=0 EndX=-74.37 EndY=9.1 EndZ=0
  constraints (12):
    c: Coincident(g0,g1)
    c: Coincident(g1,g2)
    c: Coincident(g2,g3)
    c: Coincident(g3,g0)
    c: Horizontal(g0)
    c: Horizontal(g2)
    c: Vertical(g1)
    c: Vertical(g3)
    c: DistanceX(g2,g2) = 0.6
    c: DistanceY(g3,g3) = 1
    c: DistanceX(g0,g-1) = 73.77
    c: DistanceY(g-1,g0) = 9.1
FEATURE [PartDesign::Pocket] Pocket047
  BaseFeature = -> Groove003
  Direction = (1,1,1)
  Length = 20
  Length2 = 100
  Placement = pos=(0,0,0) rot=(1,0,0;1.5708rad)
  Profile = -> Sketch068
  Type = 0
FEATURE [Sketcher::SketchObject] Sketch069
  FullyConstrained = false
  MapMode = 5
  Placement = pos=(0,0,0) rot=(0.707107,0,0.707107;3.14159rad)
  Support = -> [Pocket047]
  sketch-geometry (4):
    g0: LineSegment StartX=31.2506 StartY=8.9527 StartZ=0 EndX=32.1439 EndY=8.9527 EndZ=0
    g1: LineSegment StartX=32.1439 StartY=8.9527 StartZ=0 EndX=32.1439 EndY=-2.56247 EndZ=0
    g2: LineSegment StartX=32.1439 StartY=-2.56247 StartZ=0 EndX=31.2506 EndY=-2.56247 EndZ=0
    g3: LineSegment StartX=31.2506 StartY=-2.56247 StartZ=0 EndX=31.2506 EndY=8.9527 EndZ=0
  constraints (8):
    c: Coincident(g0,g1)
    c: Coincident(g1,g2)
    c: Coincident(g2,g3)
    c: Coincident(g3,g0)
    c: Horizontal(g0)
    c: Horizontal(g2)
    c: Vertical(g1)
    c: Vertical(g3)
FEATURE [PartDesign::Pocket] Pocket048
  BaseFeature = -> Pocket047
  Direction = (1,1,1)
  Length = 10
  Length2 = 100
  Placement = pos=(0,0,0) rot=(1,0,0;1.5708rad)
  Profile = -> Sketch069
  Type = 0
FEATURE [PartDesign::Plane] DatumPlane010  label="tape-top-surface"
  Length = 153.11
  MapMode = 5
  Placement = pos=(0,-1.09e-14,32.99) rot=(1,0,0;3.14159rad)
  ResizeMode = 0
  Support = -> [Pocket048]
  Width = 66.5277
FEATURE [Sketcher::SketchObject] Sketch070
  FullyConstrained = true
  MapMode = 5
  Placement = pos=(0,-1.09e-14,32.99) rot=(1,0,0;3.14159rad)
  Support = -> [DatumPlane010]
  sketch-geometry (7):
    g0: LineSegment StartX=75 StartY=1.6 StartZ=0 EndX=75 EndY=10.6 EndZ=0
    g1: LineSegment StartX=75 StartY=10.6 StartZ=0 EndX=76 EndY=11.6 EndZ=0
    g2: LineSegment StartX=76 StartY=11.6 StartZ=0 EndX=78 EndY=11.6 EndZ=0
    g3: LineSegment StartX=78 StartY=11.6 StartZ=0 EndX=79 EndY=10.6 EndZ=0
    g4: LineSegment StartX=79 StartY=10.6 StartZ=0 EndX=79 EndY=2.6 EndZ=0
    g5: LineSegment StartX=79 StartY=2.6 StartZ=0 EndX=78 EndY=1.6 EndZ=0
    g6: LineSegment StartX=78 StartY=1.6 StartZ=0 EndX=75 EndY=1.6 EndZ=0
  constraints (21):
    c: Vertical(g0)
    c: Coincident(g0,g1)
    c: Coincident(g1,g2)
    c: Horizontal(g2)
    c: Coincident(g2,g3)
    c: Coincident(g3,g4)
    c: Vertical(g4)
    c: Coincident(g4,g5)
    c: Coincident(g5,g6)
    c: Horizontal(g6)
    c: Coincident(g0,g6)
    c: DistanceY(g0,g1) = 10
    c: DistanceX(g0,g4) = 4
    c: Angle(g1,g2) = 2.35619
    c: Angle(g2,g3) = 2.35619
    c: Angle(g4,g5) = 2.35619
    c: DistanceX(g0,g1) = 1
    c: DistanceX(g2,g3) = 1
    c: DistanceY(g5,g4) = 1
    c: DistanceY(g-1,g0) = 1.6
    c: DistanceX(g-1,g0) = 75
FEATURE [PartDesign::Pocket] Pocket049
  BaseFeature = -> Pocket048
  Direction = (1,1,1)
  Length = 10
  Length2 = 1
  Placement = pos=(0,0,0) rot=(1,0,0;1.5708rad)
  Profile = -> Sketch070
  Reversed = true
  Type = 4
FEATURE [Sketcher::SketchObject] Sketch071
  ExternalGeometry = -> [Sketch070]
  FullyConstrained = true
  MapMode = 5
  Placement = pos=(0,-7.7e-15,31.99) rot=(0,0,1;3.14159rad)
  Support = -> [Pocket049]
  sketch-geometry (6):
    g0: LineSegment StartX=-76 StartY=1.6 StartZ=0 EndX=-76 EndY=11.6 EndZ=0
    g1: LineSegment StartX=-76 StartY=11.6 StartZ=0 EndX=-78 EndY=11.6 EndZ=0
    g2: LineSegment StartX=-78 StartY=11.6 StartZ=0 EndX=-79 EndY=10.6 EndZ=0
    g3: LineSegment StartX=-79 StartY=10.6 StartZ=0 EndX=-79 EndY=2.6 EndZ=0
    g4: LineSegment StartX=-79 StartY=2.6 StartZ=0 EndX=-78 EndY=1.6 EndZ=0
    g5: LineSegment StartX=-78 StartY=1.6 StartZ=0 EndX=-76 EndY=1.6 EndZ=0
  constraints (14):
    c: PointOnObject(g0,g-7)
    c: PointOnObject(g0,g-3)
    c: Vertical(g0)
    c: Coincident(g0,g1)
    c: Coincident(g1,g-4)
    c: Coincident(g1,g2)
    c: Coincident(g2,g-5)
    c: Coincident(g2,g3)
    c: Coincident(g3,g-6)
    c: Coincident(g3,g4)
    c: Coincident(g4,g-7)
    c: Coincident(g4,g5)
    c: Coincident(g5,g0)
    c: DistanceX(g1,g1) = 2
FEATURE [PartDesign::Pad] Pad015
  BaseFeature = -> Pocket049
  Direction = (1,1,1)
  Length = 1.3
  Length2 = 100
  Placement = pos=(0,0,0) rot=(1,0,0;1.5708rad)
  Profile = -> Sketch071
  Reversed = true
  Type = 0
FEATURE [PartDesign::Pad] Pad016
  BaseFeature = -> Pad015
  Direction = (1,1,1)
  Length = 1
  Length2 = 100
  Placement = pos=(0,0,0) rot=(1,0,0;1.5708rad)
  Profile = -> Pad015 [Face36]
  Type = 0
FEATURE [PartDesign::Pad] Pad017
  BaseFeature = -> Pad016
  Direction = (0,-1,0)
  Length = 4
  Length2 = 10
  Placement = pos=(0,0,0) rot=(1,0,0;1.5708rad)
  Profile = -> Pad016 [Face106,Face118,Face119,Face120,Face121,Face70,Face11,Face68,Face28,Face63,Face152,Face153,Face151,Face154,Face148,Face274,Face213,Face232,Face25,Face26,Face65,Face104,Face384]
  Type = 0
FEATURE [PartDesign::Pocket] Pocket050
  BaseFeature = -> Pad017
  Direction = (0,-1,-1e-16)
  Length = 4
  Length2 = 5
  Placement = pos=(0,0,0) rot=(1,0,0;1.5708rad)
  Profile = -> Pad017 [Face511]
  Type = 0
FEATURE [PartDesign::Pad] Pad018
  BaseFeature = -> Pocket050
  Direction = (0,-1,0)
  Length = 4
  Length2 = 10
  Placement = pos=(0,0,0) rot=(1,0,0;1.5708rad)
  Profile = -> Pocket050 [Face517]
  Type = 0
FEATURE [PartDesign::Pocket] Pocket051
  BaseFeature = -> Pad018
  Direction = (0,-1,2e-16)
  Length = 4
  Length2 = 5
  Placement = pos=(0,0,0) rot=(1,0,0;1.5708rad)
  Profile = -> Pad018 [Face195,Face125,Face79,Face80,Face78,Face47,Face77,Face124,Face71,Face115,Face123]
  Type = 0
FEATURE [PartDesign::Pocket] Pocket052
  BaseFeature = -> Pocket051
  Direction = (0,-1,4e-16)
  Length = 4
  Length2 = 5
  Placement = pos=(0,0,0) rot=(1,0,0;1.5708rad)
  Profile = -> Pocket051 [Face312,Face199,Face124]
  Type = 0
FEATURE [PartDesign::Pad] Pad019
  BaseFeature = -> Pocket052
  Direction = (0.21693,-0.976187,2e-15)
  Length = 10
  Length2 = 10
  Placement = pos=(0,0,0) rot=(1,0,0;1.5708rad)
  Profile = -> Pocket052 [Face2]
  ReferenceAxis = -> Pocket052 [Edge22]
  Type = 3
  UpToFace = -> Pocket052 [Face6]
FEATURE [PartDesign::Pocket] Pocket053
  BaseFeature = -> Pad019
  Direction = (0,-1,2e-16)
  Length = 4
  Length2 = 5
  Placement = pos=(0,0,0) rot=(1,0,0;1.5708rad)
  Profile = -> Pad019 [Face8,Face6,Face4,Face3,Face15]
  Type = 0
FEATURE [PartDesign::Pocket] Pocket054
  BaseFeature = -> Pocket053
  Direction = (-0.258819,0.965926,-3e-16)
  Length = 0
  Length2 = 5
  Placement = pos=(0,0,0) rot=(1,0,0;1.5708rad)
  Profile = -> Pocket053 [Face13]
  ReferenceAxis = -> Pocket053 [Edge72]
  Type = 3
  UpToFace = -> Pocket053 [Face8]
FEATURE [PartDesign::Pocket] Pocket055
  BaseFeature = -> Pocket054
  Direction = (2e-16,-1e-15,-1)
  Length = 2
  Length2 = 5
  Placement = pos=(0,0,0) rot=(1,0,0;1.5708rad)
  Profile = -> Pocket054 [Face42,Face70]
  Type = 0
FEATURE [PartDesign::Pocket] Pocket056
  BaseFeature = -> Pocket055
  Direction = (0,-1,8e-16)
  Length = 4
  Length2 = 5
  Placement = pos=(0,0,0) rot=(1,0,0;1.5708rad)
  Profile = -> Pocket055 [Face444,Face443,Face445,Face446]
  Type = 0
FEATURE [PartDesign::Pad] Pad020
  BaseFeature = -> Pocket056
  Direction = (0,-1.3e-15,-1)
  Length = 1
  Length2 = 10
  Placement = pos=(0,0,0) rot=(1,0,0;1.5708rad)
  Profile = -> Pocket056 [Face300,Face205]
  ReferenceAxis = -> Pocket056 [Edge674]
  Reversed = true
  Type = 0
FEATURE [Sketcher::SketchObject] Sketch072
  ExternalGeometry = -> [Pad020]
  FullyConstrained = false
  MapMode = 5
  Placement = pos=(0,-3.8e-15,34.9088) rot=(0,0,1;3.14159rad)
  Support = -> [Pad020]
  sketch-geometry (7):
    g0: LineSegment StartX=47.1628 StartY=19 StartZ=0 EndX=49.9958 EndY=19 EndZ=0
    g1: LineSegment StartX=49.9958 StartY=19 StartZ=0 EndX=49.9912 EndY=17 EndZ=0
    g2: LineSegment StartX=49.9912 StartY=17 StartZ=0 EndX=47.1628 EndY=19 EndZ=0
    g3: LineSegment StartX=49.9912 StartY=17 StartZ=0 EndX=53.2262 EndY=16.6749 EndZ=0
    g4: LineSegment StartX=53.2262 StartY=16.6749 StartZ=0 EndX=52.827 EndY=21.9721 EndZ=0
    g5: LineSegment StartX=52.827 StartY=21.9721 StartZ=0 EndX=47.5266 EndY=21.9721 EndZ=0
    g6: LineSegment StartX=47.5266 StartY=21.9721 StartZ=0 EndX=47.1628 EndY=19 EndZ=0
  constraints (12):
    c: Coincident(g0,g-4)
    c: Coincident(g0,g-5)
    c: Coincident(g1,g0)
    c: Coincident(g1,g-3)
    c: Coincident(g2,g1)
    c: Coincident(g2,g0)
    c: Coincident(g3,g1)
    c: Coincident(g4,g3)
    c: Coincident(g5,g4)
    c: Horizontal(g5)
    c: Coincident(g6,g5)
    c: Coincident(g6,g0)
FEATURE [PartDesign::Pocket] Pocket057
  BaseFeature = -> Pad020
  Direction = (0.707107,1.1e-15,0.707107)
  Length = 5
  Length2 = 5
  Placement = pos=(0,0,0) rot=(1,0,0;1.5708rad)
  Profile = -> Sketch072
  ReferenceAxis = -> Pad020 [Edge331]
  Reversed = true
  Type = 0
FEATURE [PartDesign::Pad] Pad021
  BaseFeature = -> Pocket057
  Direction = (0.964764,-3e-16,-0.263117)
  Length = 10
  Length2 = 10
  Placement = pos=(0,0,0) rot=(1,0,0;1.5708rad)
  Profile = -> Pocket057 [Face640]
  Type = 3
  UpToFace = -> Pocket057 [Face429]
FEATURE [Sketcher::SketchObject] Sketch073
  ExternalGeometry = -> [Pocket057]
  FullyConstrained = true
  MapMode = 5
  Placement = pos=(-11.7192,4e-16,3.19615) rot=(0.794707,0,0.606994;3.14159rad)
  Support = -> [Pocket057]
  sketch-geometry (1):
    g0: Circle CenterX=-24.5 CenterY=15 CenterZ=0 NormalX=0 NormalY=0 NormalZ=1 AngleXU=0 Radius=3.5
  constraints (3):
    c: Equal(g-3,g0)
    c: Vertical(g-3,g0)
    c: DistanceY(g-3,g0) = 4
FEATURE [PartDesign::Pocket] Pocket058
  BaseFeature = -> Pad021
  Direction = (-0.964764,4e-16,0.263117)
  Length = 2
  Length2 = 5
  Placement = pos=(0,0,0) rot=(1,0,0;1.5708rad)
  Profile = -> Sketch073
  ReferenceAxis = -> Sketch073 [N_Axis]
  Type = 0
FEATURE [PartDesign::Pocket] Pocket059
  BaseFeature = -> Pocket058
  Direction = (-0.960391,0.204137,-0.189675)
  Length = 5
  Length2 = 5
  Placement = pos=(0,0,0) rot=(1,0,0;1.5708rad)
  Profile = -> Pocket058 [Face349]
  ReferenceAxis = -> Pocket058 [Edge1201]
  Reversed = true
  Type = 1
FEATURE [PartDesign::Pocket] Pocket060
  BaseFeature = -> Pocket059
  Direction = (0,1,-1.7e-15)
  Length = 4
  Length2 = 5
  Placement = pos=(0,0,0) rot=(1,0,0;1.5708rad)
  Profile = -> Pocket059 [Face579,Face640,Face580]
  ReferenceAxis = -> Pocket059 [Edge1633]
  Reversed = true
  Type = 0
FEATURE [PartDesign::Pocket] Pocket061
  BaseFeature = -> Pocket060
  Direction = (-0.216069,1.7e-15,0.976378)
  Length = 1
  Length2 = 5
  Placement = pos=(0,0,0) rot=(1,0,0;1.5708rad)
  Profile = -> Pocket060 [Face658,Face637]
  Type = 0
FEATURE [PartDesign::Pad] Pad022
  BaseFeature = -> Pocket061
  Direction = (0.188996,-1.9e-15,-0.981978)
  Length = 1
  Length2 = 10
  Placement = pos=(0,0,0) rot=(1,0,0;1.5708rad)
  Profile = -> Pocket061 [Face639]
  Type = 0
FEATURE [Sketcher::SketchObject] Sketch074
  ExternalGeometry = -> [Pad022]
  FullyConstrained = false
  MapMode = 5
  Placement = pos=(-45.1091,-1.33e-14,-8.68189) rot=(0.636791,0,0.771037;3.14159rad)
  Support = -> [Pad022]
  sketch-geometry (8):
    g0: LineSegment StartX=26.5791 StartY=15.5611 StartZ=0 EndX=25.0208 EndY=15.5611 EndZ=0
    g1: LineSegment StartX=25.0208 StartY=15.5611 StartZ=0 EndX=25.0208 EndY=11.4084 EndZ=0
    g2: LineSegment StartX=25.0208 StartY=11.4084 StartZ=0 EndX=26.5791 EndY=11.4084 EndZ=0
    g3: LineSegment StartX=26.5791 StartY=11.4084 StartZ=0 EndX=26.5791 EndY=15.5611 EndZ=0
    g4: LineSegment StartX=26.5791 StartY=15.5611 StartZ=0 EndX=25.0208 EndY=15.5896 EndZ=0
    g5: LineSegment StartX=25.0208 StartY=15.5896 StartZ=0 EndX=25.0208 EndY=15.5611 EndZ=0
    g6: LineSegment StartX=26.5791 StartY=11.4084 StartZ=0 EndX=26.7531 EndY=10.4853 EndZ=0
    g7: LineSegment StartX=26.7531 StartY=10.4853 StartZ=0 EndX=25.0208 EndY=11.4084 EndZ=0
  constraints (17):
    c: Coincident(g0,g1)
    c: Coincident(g1,g2)
    c: Coincident(g2,g3)
    c: Coincident(g3,g0)
    c: Horizontal(g0)
    c: Horizontal(g2)
    c: Vertical(g1)
    c: Vertical(g3)
    c: Coincident(g0,g-3)
    c: Coincident(g1,g-5)
    c: Coincident(g4,g0)
    c: Coincident(g4,g-4)
    c: Coincident(g5,g4)
    c: Coincident(g5,g0)
    c: Coincident(g6,g2)
    c: Coincident(g7,g6)
    c: Coincident(g7,g1)
FEATURE [PartDesign::Pocket] Pocket062
  BaseFeature = -> Pad022
  Direction = (-0.981978,-4e-16,-0.188996)
  Length = 5
  Length2 = 5
  Placement = pos=(0,0,0) rot=(1,0,0;1.5708rad)
  Profile = -> Sketch074
  ReferenceAxis = -> Sketch074 [N_Axis]
  Type = 0
FEATURE [PartDesign::Pad] Pad023
  BaseFeature = -> Pocket062
  Direction = (0,1,-1.9e-15)
  Length = 4
  Length2 = 10
  Placement = pos=(0,0,0) rot=(1,0,0;1.5708rad)
  Profile = -> Pocket062 [Face423]
  Type = 0
FEATURE [PartDesign::Pocket] Pocket063
  BaseFeature = -> Pad023
  Direction = (0,1,-2e-15)
  Length = 4
  Length2 = 5
  Placement = pos=(0,0,0) rot=(1,0,0;1.5708rad)
  Profile = -> Pad023 [Face597]
  Type = 0
FEATURE [PartDesign::Pad] Pad024
  BaseFeature = -> Pocket063
  Direction = (0.964764,-4e-16,-0.263117)
  Length = 2
  Length2 = 10
  Placement = pos=(0,0,0) rot=(1,0,0;1.5708rad)
  Profile = -> Pocket063 [Face667]
  Type = 0
FEATURE [Sketcher::SketchObject] Sketch075
  ExternalGeometry = -> [Pad024]
  FullyConstrained = true
  MapMode = 5
  Placement = pos=(-11.7192,4.3e-15,3.19615) rot=(0.794707,0,0.606994;3.14159rad)
  Support = -> [Pad024]
  sketch-geometry (1):
    g0: Circle CenterX=-24.5 CenterY=11 CenterZ=0 NormalX=0 NormalY=0 NormalZ=1 AngleXU=0 Radius=3.5
  constraints (2):
    c: Coincident(g0,g-3)
    c: PointOnObject(g-3,g0)
FEATURE [PartDesign::Pocket] Pocket064
  BaseFeature = -> Pad024
  Direction = (-0.964764,7e-16,0.263117)
  Length = 2
  Length2 = 5
  Placement = pos=(0,0,0) rot=(1,0,0;1.5708rad)
  Profile = -> Sketch075
  ReferenceAxis = -> Sketch075 [N_Axis]
  Type = 0
FEATURE [PartDesign::Pocket] Pocket065
  BaseFeature = -> Pocket064
  Direction = (2e-16,-2.6e-15,-1)
  Length = 4
  Length2 = 5
  Placement = pos=(0,0,0) rot=(1,0,0;1.5708rad)
  Profile = -> Pocket064 [Face177,Face277,Face124,Face178,Face125,Face281]
  Type = 0
FEATURE [PartDesign::Pocket] Pocket066
  BaseFeature = -> Pocket065
  Direction = (-0.99101,-3e-16,-0.133786)
  Length = 5
  Length2 = 5
  Placement = pos=(0,0,0) rot=(1,0,0;1.5708rad)
  Profile = -> Pocket065 [Face470,Face282]
  ReferenceAxis = -> Pocket065 [Edge1226]
  Type = 1
FEATURE [PartDesign::Pocket] Pocket067
  BaseFeature = -> Pocket066
  Direction = (-0.133786,2.4e-15,0.99101)
  Length = 2
  Length2 = 5
  Placement = pos=(0,0,0) rot=(1,0,0;1.5708rad)
  Profile = -> Pocket066 [Face426,Face422]
  Type = 0
FEATURE [Sketcher::SketchObject] Sketch076
  ExternalGeometry = -> [Pocket067]
  FullyConstrained = false
  MapMode = 5
  Placement = pos=(0,-19,-4.2e-15) rot=(1,0,0;1.5708rad)
  Support = -> [Pocket067]
  sketch-geometry (9):
    g0: LineSegment StartX=25.25 StartY=-1.4e-15 StartZ=0 EndX=25.25 EndY=-2.85786 EndZ=0
    g1: LineSegment StartX=28.1789 StartY=-9.92893 StartZ=0 EndX=38.25 EndY=-20 EndZ=0
    g2: LineSegment StartX=38.25 StartY=-20 StartZ=0 EndX=39.849 EndY=-21.5991 EndZ=0
    g3: LineSegment StartX=36.4455 StartY=-26.5177 StartZ=0 EndX=11.2198 EndY=-15.094 EndZ=0
    g4: LineSegment StartX=10.334 StartY=-10.7072 StartZ=0 EndX=20.25 EndY=-1.8e-15 EndZ=0
    g5: LineSegment StartX=20.25 StartY=-1.8e-15 StartZ=0 EndX=25.25 EndY=-1.4e-15 EndZ=0
    g6: ArcOfCircle CenterX=12.3577 CenterY=-12.5814 CenterZ=0 NormalX=0 NormalY=0 NormalZ=1 AngleXU=0 Radius=2.75824 StartAngle=2.39454 EndAngle=4.28716
    g7: ArcOfCircle CenterX=37.6996 CenterY=-23.7485 CenterZ=0 NormalX=0 NormalY=0 NormalZ=1 AngleXU=0 Radius=3.03984 StartAngle=4.28716 EndAngle=7.06858
    g8: ArcOfCircle CenterX=35.25 CenterY=-2.85786 CenterZ=0 NormalX=0 NormalY=0 NormalZ=1 AngleXU=0 Radius=10 StartAngle=3.14159 EndAngle=3.92699
  constraints (15):
    c: Coincident(g0,g-7)
    c: Coincident(g0,g-7)
    c: Coincident(g1,g-5)
    c: Coincident(g1,g-6)
    c: Coincident(g4,g-3)
    c: Coincident(g5,g4)
    c: Coincident(g5,g0)
    c: Tangent(g3,g6) = 1.5708
    c: Tangent(g4,g6) = 1.5708
    c: Tangent(g3,g7) = 1.5708
    c: Tangent(g2,g7) = 1.5708
    c: Coincident(g8,g0)
    c: Coincident(g8,g1)
    c: Tangent(g8,g-4)
    c: Tangent(g2,g1) = -1.5708
FEATURE [PartDesign::Pocket] Pocket068
  BaseFeature = -> Pocket067
  Direction = (0,1,-2.9e-15)
  Length = 4
  Length2 = 5
  Placement = pos=(0,0,0) rot=(1,0,0;1.5708rad)
  Profile = -> Sketch076
  ReferenceAxis = -> Sketch076 [N_Axis]
  Type = 0
FEATURE [PartDesign::Pocket] Pocket069
  BaseFeature = -> Pocket068
  Direction = (0.707107,-2.1e-15,-0.707107)
  Length = 5
  Length2 = 5
  Placement = pos=(0,0,0) rot=(1,0,0;1.5708rad)
  Profile = -> Pocket068 [Face179,Face286]
  ReferenceAxis = -> Pocket068 [Edge375]
  Type = 1
FEATURE [PartDesign::Pocket] Pocket070
  BaseFeature = -> Pocket069
  Direction = (0,-1,2.9e-15)
  Length = 5
  Length2 = 5
  Placement = pos=(0,0,0) rot=(1,0,0;1.5708rad)
  Profile = -> Pocket069 [Face128,Face464]
  Type = 2
FEATURE [PartDesign::Pad] Pad025
  BaseFeature = -> Pocket070
  Direction = (-8.1282,2.1e-15,-19.6232)
  Length = 0.2
  Length2 = 10
  Placement = pos=(0,0,0) rot=(1,0,0;1.5708rad)
  Profile = -> Pocket070 [Face74,Face82,Face44,Face43,Face81,Face80,Face112]
  Type = 0
FEATURE [PartDesign::Pad] Pad026
  BaseFeature = -> Pad025
  Direction = (-1,0,0)
  Length = 10
  Length2 = 10
  Placement = pos=(0,0,0) rot=(1,0,0;1.5708rad)
  Profile = -> Pad025 [Face120]
  ReferenceAxis = -> Pad025 [Edge94]
  Type = 3
  UpToFace = -> Pad025 [Face176]
FEATURE [PartDesign::Pad] Pad027
  BaseFeature = -> Pad026
  Direction = (1,0,0)
  Length = 10
  Length2 = 10
  Placement = pos=(0,0,0) rot=(1,0,0;1.5708rad)
  Profile = -> Pad026 [Face176,Face225]
  ReferenceAxis = -> Pad026 [Edge356]
  Type = 3
  UpToFace = -> Pad026 [Face174]
FEATURE [PartDesign::Pad] Pad028
  BaseFeature = -> Pad027
  Direction = (0,0,-1)
  Length = 0.2
  Length2 = 10
  Placement = pos=(0,0,0) rot=(1,0,0;1.5708rad)
  Profile = -> Pad027 [Face64,Face173,Face23,Face38,Face37]
  Type = 0
FEATURE [PartDesign::Pocket] Pocket071
  BaseFeature = -> Pad028
  Direction = (-1,0,0)
  Length = 5
  Length2 = 5
  Placement = pos=(0,0,0) rot=(1,0,0;1.5708rad)
  Profile = -> Pad028 [Face77]
  Type = 0
FEATURE [PartDesign::Pocket] Pocket072
  BaseFeature = -> Pocket071
  Direction = (-0.707107,-4e-16,-0.707107)
  Length = 5
  Length2 = 5
  Placement = pos=(0,0,0) rot=(1,0,0;1.5708rad)
  Profile = -> Pocket071 [Face81,Face139]
  ReferenceAxis = -> Pocket071 [Edge48]
  Type = 0
FEATURE [PartDesign::Pocket] Pocket073
  BaseFeature = -> Pocket072
  Direction = (0,1,-3e-16)
  Length = 5
  Length2 = 5
  Placement = pos=(0,0,0) rot=(1,0,0;1.5708rad)
  Profile = -> Pocket072 [Face188,Face434,Face138]
  Type = 1
FEATURE [PartDesign::Pad] Pad029
  BaseFeature = -> Pocket073
  Direction = (0.707107,5e-16,0.707107)
  Length = 1
  Length2 = 10
  Placement = pos=(0,0,0) rot=(1,0,0;1.5708rad)
  Profile = -> Pocket073 [Face77]
  ReferenceAxis = -> Pocket073 [Edge48]
  Reversed = true
  Type = 0
FEATURE [PartDesign::Pocket] Pocket074
  BaseFeature = -> Pad029
  Direction = (0.707107,-4e-16,-0.707107)
  Length = 5
  Length2 = 5
  Placement = pos=(0,0,0) rot=(1,0,0;1.5708rad)
  Profile = -> Pad029 [Face165]
  Type = 0
FEATURE [PartDesign::Body] Body
  Group = -> [Sketch,Pad,Sketch001,Pocket,Sketch002,DatumPlane002,Pocket001,Sketch003,Sketch014,Sketch015,Groove,Sketch016,DatumPlane004,Pocket009,Pocket002,Sketch004,Pocket003,Sketch005,Pad001,Sketch006,Pocket004,Sketch007,Pocket005,Sketch008,Pocket006,Sketch009,Pocket007,Sketch010,Pocket008,DatumPlane,Sketch011,Pad002,Sketch017,Pocket010,Fillet,Chamfer,DatumPlane003,Sketch018,Groove001,Sketch019,Pocket011,+163 more]
  Origin = -> Origin
  Tip = -> Pocket074
